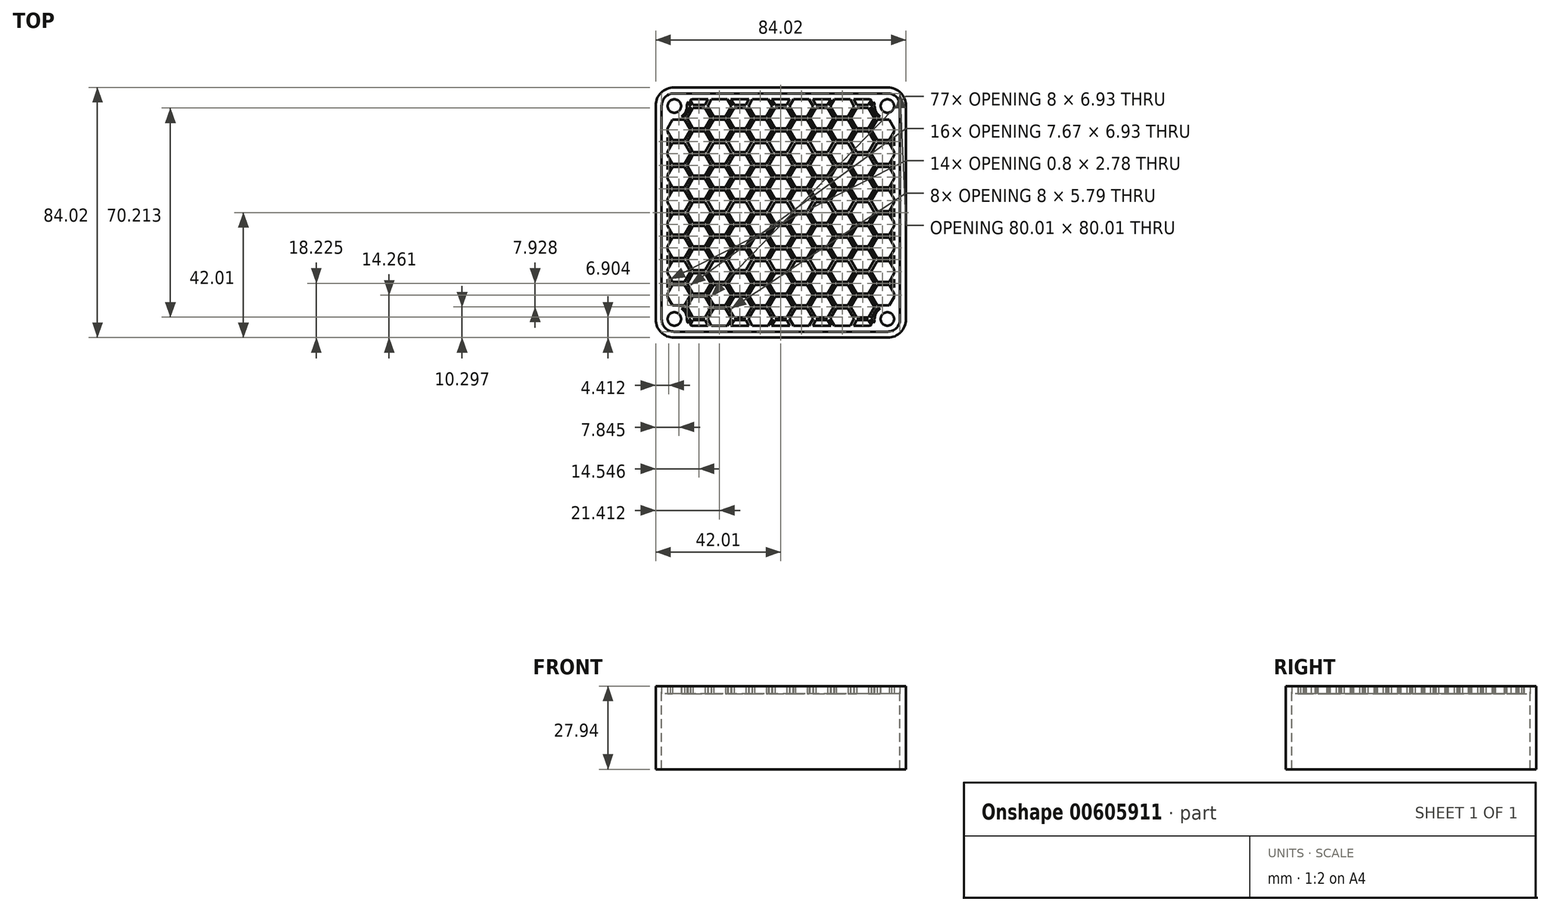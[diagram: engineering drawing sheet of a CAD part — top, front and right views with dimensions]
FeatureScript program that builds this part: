
annotation { "Feature Type Name" : "Feature", "Feature Type Description" : "" }
export const myFeature = defineFeature(function(context is Context, id is Id, definition is map)
    precondition{}
    {
        {
            var Q0;
            Q0=qCreatedBy(makeId("Top.planeOp"),FACE);
            var sketch = newSketch(context, id + "F0", { "sketchPlane" : qUnion([Q0])});
            skLineSegment(sketch, "E0", {"start": v(11.73, 28.25) * mm, "end": v(9.73, 31.71) * mm});
            skLineSegment(sketch, "E1", {"start": v(-16.6, 27.75) * mm, "end": v(-18.6, 24.28) * mm});
            skLineSegment(sketch, "E2", {"start": v(-2, -3.46) * mm, "end": v(2, -3.46) * mm});
            skLineSegment(sketch, "E3", {"start": v(2, -3.46) * mm, "end": v(4, 0) * mm});
            skLineSegment(sketch, "E4", {"start": v(4, 0) * mm, "end": v(2, 3.46) * mm});
            skLineSegment(sketch, "E5", {"start": v(2, 3.46) * mm, "end": v(-2, 3.46) * mm});
            skLineSegment(sketch, "E6", {"start": v(-2, 3.46) * mm, "end": v(-4, 0) * mm});
            skLineSegment(sketch, "E7", {"start": v(-4, 0) * mm, "end": v(-2, -3.46) * mm});
            skLineSegment(sketch, "E8", {"start": v(-2.87, 3.96) * mm, "end": v(-4.87, 0.5) * mm});
            skLineSegment(sketch, "E9", {"start": v(-4.87, -0.5) * mm, "end": v(-2.87, -3.96) * mm});
            skLineSegment(sketch, "E10", {"start": v(-2, 4.46) * mm, "end": v(2, 4.46) * mm});
            skLineSegment(sketch, "E11", {"start": v(2, 4.46) * mm, "end": v(4, 7.93) * mm});
            skLineSegment(sketch, "E12", {"start": v(4, 7.93) * mm, "end": v(2, 11.4) * mm});
            skLineSegment(sketch, "E13", {"start": v(2, 11.4) * mm, "end": v(-2, 11.4) * mm});
            skLineSegment(sketch, "E14", {"start": v(-2, 11.4) * mm, "end": v(-4, 7.93) * mm});
            skLineSegment(sketch, "E15", {"start": v(-4, 7.93) * mm, "end": v(-2, 4.46) * mm});
            skLineSegment(sketch, "E16", {"start": v(-2, 12.4) * mm, "end": v(2, 12.4) * mm});
            skLineSegment(sketch, "E17", {"start": v(2, 12.4) * mm, "end": v(4, 15.86) * mm});
            skLineSegment(sketch, "E18", {"start": v(4, 15.86) * mm, "end": v(2, 19.32) * mm});
            skLineSegment(sketch, "E19", {"start": v(2, 19.32) * mm, "end": v(-2, 19.32) * mm});
            skLineSegment(sketch, "E20", {"start": v(-2, 19.32) * mm, "end": v(-4, 15.86) * mm});
            skLineSegment(sketch, "E21", {"start": v(-4, 15.86) * mm, "end": v(-2, 12.4) * mm});
            skLineSegment(sketch, "E22", {"start": v(-2, 20.32) * mm, "end": v(2, 20.32) * mm});
            skLineSegment(sketch, "E23", {"start": v(2, 20.32) * mm, "end": v(4, 23.78) * mm});
            skLineSegment(sketch, "E24", {"start": v(4, 23.78) * mm, "end": v(2, 27.25) * mm});
            skLineSegment(sketch, "E25", {"start": v(2, 27.25) * mm, "end": v(-2, 27.25) * mm});
            skLineSegment(sketch, "E26", {"start": v(-2, 27.25) * mm, "end": v(-4, 23.78) * mm});
            skLineSegment(sketch, "E27", {"start": v(-4, 23.78) * mm, "end": v(-2, 20.32) * mm});
            skLineSegment(sketch, "E28", {"start": v(-2, 28.25) * mm, "end": v(2, 28.25) * mm});
            skLineSegment(sketch, "E29", {"start": v(2, 28.25) * mm, "end": v(4, 31.71) * mm});
            skLineSegment(sketch, "E30", {"start": v(4, 31.71) * mm, "end": v(2, 35.18) * mm});
            skLineSegment(sketch, "E31", {"start": v(2, 35.18) * mm, "end": v(-2, 35.18) * mm});
            skLineSegment(sketch, "E32", {"start": v(-2, 35.18) * mm, "end": v(-4, 31.71) * mm});
            skLineSegment(sketch, "E33", {"start": v(-4, 31.71) * mm, "end": v(-2, 28.25) * mm});
            skLineSegment(sketch, "E34", {"start": v(-2, 36.18) * mm, "end": v(2, 36.18) * mm});
            skLineSegment(sketch, "E35", {"start": v(-2, -11.4) * mm, "end": v(2, -11.4) * mm});
            skLineSegment(sketch, "E36", {"start": v(2, -11.4) * mm, "end": v(4, -7.93) * mm});
            skLineSegment(sketch, "E37", {"start": v(4, -7.93) * mm, "end": v(2, -4.46) * mm});
            skLineSegment(sketch, "E38", {"start": v(2, -4.46) * mm, "end": v(-2, -4.46) * mm});
            skLineSegment(sketch, "E39", {"start": v(-2, -4.46) * mm, "end": v(-4, -7.93) * mm});
            skLineSegment(sketch, "E40", {"start": v(-4, -7.93) * mm, "end": v(-2, -11.4) * mm});
            skLineSegment(sketch, "E41", {"start": v(-2, -19.32) * mm, "end": v(2, -19.32) * mm});
            skLineSegment(sketch, "E42", {"start": v(2, -19.32) * mm, "end": v(4, -15.86) * mm});
            skLineSegment(sketch, "E43", {"start": v(4, -15.86) * mm, "end": v(2, -12.4) * mm});
            skLineSegment(sketch, "E44", {"start": v(2, -12.4) * mm, "end": v(-2, -12.4) * mm});
            skLineSegment(sketch, "E45", {"start": v(-2, -12.4) * mm, "end": v(-4, -15.86) * mm});
            skLineSegment(sketch, "E46", {"start": v(-4, -15.86) * mm, "end": v(-2, -19.32) * mm});
            skLineSegment(sketch, "E47", {"start": v(-2, -27.25) * mm, "end": v(2, -27.25) * mm});
            skLineSegment(sketch, "E48", {"start": v(2, -27.25) * mm, "end": v(4, -23.78) * mm});
            skLineSegment(sketch, "E49", {"start": v(4, -23.78) * mm, "end": v(2, -20.32) * mm});
            skLineSegment(sketch, "E50", {"start": v(2, -20.32) * mm, "end": v(-2, -20.32) * mm});
            skLineSegment(sketch, "E51", {"start": v(-2, -20.32) * mm, "end": v(-4, -23.78) * mm});
            skLineSegment(sketch, "E52", {"start": v(-4, -23.78) * mm, "end": v(-2, -27.25) * mm});
            skLineSegment(sketch, "E53", {"start": v(-2, -35.18) * mm, "end": v(2, -35.18) * mm});
            skLineSegment(sketch, "E54", {"start": v(2, -35.18) * mm, "end": v(4, -31.71) * mm});
            skLineSegment(sketch, "E55", {"start": v(4, -31.71) * mm, "end": v(2, -28.25) * mm});
            skLineSegment(sketch, "E56", {"start": v(2, -28.25) * mm, "end": v(-2, -28.25) * mm});
            skLineSegment(sketch, "E57", {"start": v(-2, -28.25) * mm, "end": v(-4, -31.71) * mm});
            skLineSegment(sketch, "E58", {"start": v(-4, -31.71) * mm, "end": v(-2, -35.18) * mm});
            skLineSegment(sketch, "E59", {"start": v(2, -36.18) * mm, "end": v(-2, -36.18) * mm});
            skLineSegment(sketch, "E60", {"start": v(4.87, -7.43) * mm, "end": v(8.87, -7.43) * mm});
            skLineSegment(sketch, "E61", {"start": v(8.87, -7.43) * mm, "end": v(10.87, -3.96) * mm});
            skLineSegment(sketch, "E62", {"start": v(10.87, -3.96) * mm, "end": v(8.87, -0.5) * mm});
            skLineSegment(sketch, "E63", {"start": v(8.87, -0.5) * mm, "end": v(4.87, -0.5) * mm});
            skLineSegment(sketch, "E64", {"start": v(4.87, -0.5) * mm, "end": v(2.87, -3.96) * mm});
            skLineSegment(sketch, "E65", {"start": v(2.87, -3.96) * mm, "end": v(4.87, -7.43) * mm});
            skLineSegment(sketch, "E66", {"start": v(4, 0) * mm, "end": v(2, -3.46) * mm});
            skLineSegment(sketch, "E67", {"start": v(2, -4.46) * mm, "end": v(4, -7.93) * mm});
            skLineSegment(sketch, "E68", {"start": v(4.87, 0.5) * mm, "end": v(8.87, 0.5) * mm});
            skLineSegment(sketch, "E69", {"start": v(8.87, 0.5) * mm, "end": v(10.87, 3.96) * mm});
            skLineSegment(sketch, "E70", {"start": v(10.87, 3.96) * mm, "end": v(8.87, 7.43) * mm});
            skLineSegment(sketch, "E71", {"start": v(8.87, 7.43) * mm, "end": v(4.87, 7.43) * mm});
            skLineSegment(sketch, "E72", {"start": v(4.87, 7.43) * mm, "end": v(2.87, 3.96) * mm});
            skLineSegment(sketch, "E73", {"start": v(2.87, 3.96) * mm, "end": v(4.87, 0.5) * mm});
            skLineSegment(sketch, "E74", {"start": v(4.87, 8.43) * mm, "end": v(8.87, 8.43) * mm});
            skLineSegment(sketch, "E75", {"start": v(8.87, 8.43) * mm, "end": v(10.87, 11.9) * mm});
            skLineSegment(sketch, "E76", {"start": v(10.87, 11.9) * mm, "end": v(8.87, 15.36) * mm});
            skLineSegment(sketch, "E77", {"start": v(8.87, 15.36) * mm, "end": v(4.87, 15.36) * mm});
            skLineSegment(sketch, "E78", {"start": v(4.87, 15.36) * mm, "end": v(2.87, 11.9) * mm});
            skLineSegment(sketch, "E79", {"start": v(2.87, 11.9) * mm, "end": v(4.87, 8.43) * mm});
            skLineSegment(sketch, "E80", {"start": v(4.87, 16.36) * mm, "end": v(8.87, 16.36) * mm});
            skLineSegment(sketch, "E81", {"start": v(8.87, 16.36) * mm, "end": v(10.87, 19.82) * mm});
            skLineSegment(sketch, "E82", {"start": v(10.87, 19.82) * mm, "end": v(8.87, 23.28) * mm});
            skLineSegment(sketch, "E83", {"start": v(8.87, 23.28) * mm, "end": v(4.87, 23.28) * mm});
            skLineSegment(sketch, "E84", {"start": v(4.87, 23.28) * mm, "end": v(2.87, 19.82) * mm});
            skLineSegment(sketch, "E85", {"start": v(2.87, 19.82) * mm, "end": v(4.87, 16.36) * mm});
            skLineSegment(sketch, "E86", {"start": v(4.87, 24.28) * mm, "end": v(8.87, 24.28) * mm});
            skLineSegment(sketch, "E87", {"start": v(8.87, 24.28) * mm, "end": v(10.87, 27.75) * mm});
            skLineSegment(sketch, "E88", {"start": v(10.87, 27.75) * mm, "end": v(8.87, 31.21) * mm});
            skLineSegment(sketch, "E89", {"start": v(8.87, 31.21) * mm, "end": v(4.87, 31.21) * mm});
            skLineSegment(sketch, "E90", {"start": v(4.87, 31.21) * mm, "end": v(2.87, 27.75) * mm});
            skLineSegment(sketch, "E91", {"start": v(2.87, 27.75) * mm, "end": v(4.87, 24.28) * mm});
            skLineSegment(sketch, "E92", {"start": v(4.87, 32.21) * mm, "end": v(8.87, 32.21) * mm});
            skLineSegment(sketch, "E93", {"start": v(8.87, 32.21) * mm, "end": v(10.87, 35.68) * mm});
            skLineSegment(sketch, "E94", {"start": v(2.87, 35.68) * mm, "end": v(4.87, 32.21) * mm});
            skLineSegment(sketch, "E95", {"start": v(4.87, -15.36) * mm, "end": v(8.87, -15.36) * mm});
            skLineSegment(sketch, "E96", {"start": v(8.87, -15.36) * mm, "end": v(10.87, -11.9) * mm});
            skLineSegment(sketch, "E97", {"start": v(10.87, -11.9) * mm, "end": v(8.87, -8.43) * mm});
            skLineSegment(sketch, "E98", {"start": v(8.87, -8.43) * mm, "end": v(4.87, -8.43) * mm});
            skLineSegment(sketch, "E99", {"start": v(4.87, -8.43) * mm, "end": v(2.87, -11.9) * mm});
            skLineSegment(sketch, "E100", {"start": v(2.87, -11.9) * mm, "end": v(4.87, -15.36) * mm});
            skLineSegment(sketch, "E101", {"start": v(4.87, -23.28) * mm, "end": v(8.87, -23.28) * mm});
            skLineSegment(sketch, "E102", {"start": v(8.87, -23.28) * mm, "end": v(10.87, -19.82) * mm});
            skLineSegment(sketch, "E103", {"start": v(10.87, -19.82) * mm, "end": v(8.87, -16.36) * mm});
            skLineSegment(sketch, "E104", {"start": v(8.87, -16.36) * mm, "end": v(4.87, -16.36) * mm});
            skLineSegment(sketch, "E105", {"start": v(4.87, -16.36) * mm, "end": v(2.87, -19.82) * mm});
            skLineSegment(sketch, "E106", {"start": v(2.87, -19.82) * mm, "end": v(4.87, -23.28) * mm});
            skLineSegment(sketch, "E107", {"start": v(4.87, -31.21) * mm, "end": v(8.87, -31.21) * mm});
            skLineSegment(sketch, "E108", {"start": v(8.87, -31.21) * mm, "end": v(10.87, -27.75) * mm});
            skLineSegment(sketch, "E109", {"start": v(10.87, -27.75) * mm, "end": v(8.87, -24.28) * mm});
            skLineSegment(sketch, "E110", {"start": v(8.87, -24.28) * mm, "end": v(4.87, -24.28) * mm});
            skLineSegment(sketch, "E111", {"start": v(4.87, -24.28) * mm, "end": v(2.87, -27.75) * mm});
            skLineSegment(sketch, "E112", {"start": v(2.87, -27.75) * mm, "end": v(4.87, -31.21) * mm});
            skLineSegment(sketch, "E113", {"start": v(10.87, -35.68) * mm, "end": v(8.87, -32.21) * mm});
            skLineSegment(sketch, "E114", {"start": v(8.87, -32.21) * mm, "end": v(4.87, -32.21) * mm});
            skLineSegment(sketch, "E115", {"start": v(4.87, -32.21) * mm, "end": v(2.87, -35.68) * mm});
            skLineSegment(sketch, "E116", {"start": v(-15.73, -3.46) * mm, "end": v(-11.73, -3.46) * mm});
            skLineSegment(sketch, "E117", {"start": v(-11.73, -3.46) * mm, "end": v(-9.73, 0) * mm});
            skLineSegment(sketch, "E118", {"start": v(-9.73, 0) * mm, "end": v(-11.73, 3.46) * mm});
            skLineSegment(sketch, "E119", {"start": v(-11.73, 3.46) * mm, "end": v(-15.73, 3.46) * mm});
            skLineSegment(sketch, "E120", {"start": v(-15.73, 3.46) * mm, "end": v(-17.73, 0) * mm});
            skLineSegment(sketch, "E121", {"start": v(-17.73, 0) * mm, "end": v(-15.73, -3.46) * mm});
            skLineSegment(sketch, "E122", {"start": v(-15.73, 4.46) * mm, "end": v(-11.73, 4.46) * mm});
            skLineSegment(sketch, "E123", {"start": v(-11.73, 4.46) * mm, "end": v(-9.73, 7.93) * mm});
            skLineSegment(sketch, "E124", {"start": v(-9.73, 7.93) * mm, "end": v(-11.73, 11.4) * mm});
            skLineSegment(sketch, "E125", {"start": v(-11.73, 11.4) * mm, "end": v(-15.73, 11.4) * mm});
            skLineSegment(sketch, "E126", {"start": v(-15.73, 11.4) * mm, "end": v(-17.73, 7.93) * mm});
            skLineSegment(sketch, "E127", {"start": v(-17.73, 7.93) * mm, "end": v(-15.73, 4.46) * mm});
            skLineSegment(sketch, "E128", {"start": v(-15.73, 12.4) * mm, "end": v(-11.73, 12.4) * mm});
            skLineSegment(sketch, "E129", {"start": v(-11.73, 12.4) * mm, "end": v(-9.73, 15.86) * mm});
            skLineSegment(sketch, "E130", {"start": v(-9.73, 15.86) * mm, "end": v(-11.73, 19.32) * mm});
            skLineSegment(sketch, "E131", {"start": v(-11.73, 19.32) * mm, "end": v(-15.73, 19.32) * mm});
            skLineSegment(sketch, "E132", {"start": v(-15.73, 19.32) * mm, "end": v(-17.73, 15.86) * mm});
            skLineSegment(sketch, "E133", {"start": v(-17.73, 15.86) * mm, "end": v(-15.73, 12.4) * mm});
            skLineSegment(sketch, "E134", {"start": v(-15.73, 20.32) * mm, "end": v(-11.73, 20.32) * mm});
            skLineSegment(sketch, "E135", {"start": v(-11.73, 20.32) * mm, "end": v(-9.73, 23.78) * mm});
            skLineSegment(sketch, "E136", {"start": v(-9.73, 23.78) * mm, "end": v(-11.73, 27.25) * mm});
            skLineSegment(sketch, "E137", {"start": v(-11.73, 27.25) * mm, "end": v(-15.73, 27.25) * mm});
            skLineSegment(sketch, "E138", {"start": v(-15.73, 27.25) * mm, "end": v(-17.73, 23.78) * mm});
            skLineSegment(sketch, "E139", {"start": v(-17.73, 23.78) * mm, "end": v(-15.73, 20.32) * mm});
            skLineSegment(sketch, "E140", {"start": v(-15.73, 28.25) * mm, "end": v(-11.73, 28.25) * mm});
            skLineSegment(sketch, "E141", {"start": v(-11.73, 28.25) * mm, "end": v(-9.73, 31.71) * mm});
            skLineSegment(sketch, "E142", {"start": v(-9.73, 31.71) * mm, "end": v(-11.73, 35.18) * mm});
            skLineSegment(sketch, "E143", {"start": v(-11.73, 35.18) * mm, "end": v(-15.73, 35.18) * mm});
            skLineSegment(sketch, "E144", {"start": v(-15.73, 35.18) * mm, "end": v(-17.73, 31.71) * mm});
            skLineSegment(sketch, "E145", {"start": v(-17.73, 31.71) * mm, "end": v(-15.73, 28.25) * mm});
            skLineSegment(sketch, "E146", {"start": v(-15.73, 36.18) * mm, "end": v(-11.73, 36.18) * mm});
            skLineSegment(sketch, "E147", {"start": v(-15.73, -11.4) * mm, "end": v(-11.73, -11.4) * mm});
            skLineSegment(sketch, "E148", {"start": v(-11.73, -11.4) * mm, "end": v(-9.73, -7.93) * mm});
            skLineSegment(sketch, "E149", {"start": v(-9.73, -7.93) * mm, "end": v(-11.73, -4.46) * mm});
            skLineSegment(sketch, "E150", {"start": v(-11.73, -4.46) * mm, "end": v(-15.73, -4.46) * mm});
            skLineSegment(sketch, "E151", {"start": v(-15.73, -4.46) * mm, "end": v(-17.73, -7.93) * mm});
            skLineSegment(sketch, "E152", {"start": v(-17.73, -7.93) * mm, "end": v(-15.73, -11.4) * mm});
            skLineSegment(sketch, "E153", {"start": v(-15.73, -19.32) * mm, "end": v(-11.73, -19.32) * mm});
            skLineSegment(sketch, "E154", {"start": v(-11.73, -19.32) * mm, "end": v(-9.73, -15.86) * mm});
            skLineSegment(sketch, "E155", {"start": v(-9.73, -15.86) * mm, "end": v(-11.73, -12.4) * mm});
            skLineSegment(sketch, "E156", {"start": v(-11.73, -12.4) * mm, "end": v(-15.73, -12.4) * mm});
            skLineSegment(sketch, "E157", {"start": v(-15.73, -12.4) * mm, "end": v(-17.73, -15.86) * mm});
            skLineSegment(sketch, "E158", {"start": v(-17.73, -15.86) * mm, "end": v(-15.73, -19.32) * mm});
            skLineSegment(sketch, "E159", {"start": v(-15.73, -27.25) * mm, "end": v(-11.73, -27.25) * mm});
            skLineSegment(sketch, "E160", {"start": v(-11.73, -27.25) * mm, "end": v(-9.73, -23.78) * mm});
            skLineSegment(sketch, "E161", {"start": v(-9.73, -23.78) * mm, "end": v(-11.73, -20.32) * mm});
            skLineSegment(sketch, "E162", {"start": v(-11.73, -20.32) * mm, "end": v(-15.73, -20.32) * mm});
            skLineSegment(sketch, "E163", {"start": v(-15.73, -20.32) * mm, "end": v(-17.73, -23.78) * mm});
            skLineSegment(sketch, "E164", {"start": v(-17.73, -23.78) * mm, "end": v(-15.73, -27.25) * mm});
            skLineSegment(sketch, "E165", {"start": v(-15.73, -35.18) * mm, "end": v(-11.73, -35.18) * mm});
            skLineSegment(sketch, "E166", {"start": v(-11.73, -35.18) * mm, "end": v(-9.73, -31.71) * mm});
            skLineSegment(sketch, "E167", {"start": v(-9.73, -31.71) * mm, "end": v(-11.73, -28.25) * mm});
            skLineSegment(sketch, "E168", {"start": v(-11.73, -28.25) * mm, "end": v(-15.73, -28.25) * mm});
            skLineSegment(sketch, "E169", {"start": v(-15.73, -28.25) * mm, "end": v(-17.73, -31.71) * mm});
            skLineSegment(sketch, "E170", {"start": v(-17.73, -31.71) * mm, "end": v(-15.73, -35.18) * mm});
            skLineSegment(sketch, "E171", {"start": v(-11.73, -36.18) * mm, "end": v(-15.73, -36.18) * mm});
            skLineSegment(sketch, "E172", {"start": v(-8.87, -7.43) * mm, "end": v(-4.87, -7.43) * mm});
            skLineSegment(sketch, "E173", {"start": v(-4.87, -7.43) * mm, "end": v(-2.87, -3.96) * mm});
            skLineSegment(sketch, "E174", {"start": v(-4.87, -0.5) * mm, "end": v(-8.87, -0.5) * mm});
            skLineSegment(sketch, "E175", {"start": v(-8.87, -0.5) * mm, "end": v(-10.87, -3.96) * mm});
            skLineSegment(sketch, "E176", {"start": v(-10.87, -3.96) * mm, "end": v(-8.87, -7.43) * mm});
            skLineSegment(sketch, "E177", {"start": v(-9.73, 0) * mm, "end": v(-11.73, -3.46) * mm});
            skLineSegment(sketch, "E178", {"start": v(-11.73, -4.46) * mm, "end": v(-9.73, -7.93) * mm});
            skLineSegment(sketch, "E179", {"start": v(-8.87, 0.5) * mm, "end": v(-4.87, 0.5) * mm});
            skLineSegment(sketch, "E180", {"start": v(-2.87, 3.96) * mm, "end": v(-4.87, 7.43) * mm});
            skLineSegment(sketch, "E181", {"start": v(-4.87, 7.43) * mm, "end": v(-8.87, 7.43) * mm});
            skLineSegment(sketch, "E182", {"start": v(-8.87, 7.43) * mm, "end": v(-10.87, 3.96) * mm});
            skLineSegment(sketch, "E183", {"start": v(-10.87, 3.96) * mm, "end": v(-8.87, 0.5) * mm});
            skLineSegment(sketch, "E184", {"start": v(-8.87, 8.43) * mm, "end": v(-4.87, 8.43) * mm});
            skLineSegment(sketch, "E185", {"start": v(-4.87, 8.43) * mm, "end": v(-2.87, 11.9) * mm});
            skLineSegment(sketch, "E186", {"start": v(-2.87, 11.9) * mm, "end": v(-4.87, 15.36) * mm});
            skLineSegment(sketch, "E187", {"start": v(-4.87, 15.36) * mm, "end": v(-8.87, 15.36) * mm});
            skLineSegment(sketch, "E188", {"start": v(-8.87, 15.36) * mm, "end": v(-10.87, 11.9) * mm});
            skLineSegment(sketch, "E189", {"start": v(-10.87, 11.9) * mm, "end": v(-8.87, 8.43) * mm});
            skLineSegment(sketch, "E190", {"start": v(-8.87, 16.36) * mm, "end": v(-4.87, 16.36) * mm});
            skLineSegment(sketch, "E191", {"start": v(-4.87, 16.36) * mm, "end": v(-2.87, 19.82) * mm});
            skLineSegment(sketch, "E192", {"start": v(-2.87, 19.82) * mm, "end": v(-4.87, 23.28) * mm});
            skLineSegment(sketch, "E193", {"start": v(-4.87, 23.28) * mm, "end": v(-8.87, 23.28) * mm});
            skLineSegment(sketch, "E194", {"start": v(-8.87, 23.28) * mm, "end": v(-10.87, 19.82) * mm});
            skLineSegment(sketch, "E195", {"start": v(-10.87, 19.82) * mm, "end": v(-8.87, 16.36) * mm});
            skLineSegment(sketch, "E196", {"start": v(-8.87, 24.28) * mm, "end": v(-4.87, 24.28) * mm});
            skLineSegment(sketch, "E197", {"start": v(-4.87, 24.28) * mm, "end": v(-2.87, 27.75) * mm});
            skLineSegment(sketch, "E198", {"start": v(-2.87, 27.75) * mm, "end": v(-4.87, 31.21) * mm});
            skLineSegment(sketch, "E199", {"start": v(-4.87, 31.21) * mm, "end": v(-8.87, 31.21) * mm});
            skLineSegment(sketch, "E200", {"start": v(-8.87, 31.21) * mm, "end": v(-10.87, 27.75) * mm});
            skLineSegment(sketch, "E201", {"start": v(-10.87, 27.75) * mm, "end": v(-8.87, 24.28) * mm});
            skLineSegment(sketch, "E202", {"start": v(-8.87, 32.21) * mm, "end": v(-4.87, 32.21) * mm});
            skLineSegment(sketch, "E203", {"start": v(-4.87, 32.21) * mm, "end": v(-2.87, 35.68) * mm});
            skLineSegment(sketch, "E204", {"start": v(-10.87, 35.68) * mm, "end": v(-8.87, 32.21) * mm});
            skLineSegment(sketch, "E205", {"start": v(-8.87, -15.36) * mm, "end": v(-4.87, -15.36) * mm});
            skLineSegment(sketch, "E206", {"start": v(-4.87, -15.36) * mm, "end": v(-2.87, -11.9) * mm});
            skLineSegment(sketch, "E207", {"start": v(-2.87, -11.9) * mm, "end": v(-4.87, -8.43) * mm});
            skLineSegment(sketch, "E208", {"start": v(-4.87, -8.43) * mm, "end": v(-8.87, -8.43) * mm});
            skLineSegment(sketch, "E209", {"start": v(-8.87, -8.43) * mm, "end": v(-10.87, -11.9) * mm});
            skLineSegment(sketch, "E210", {"start": v(-10.87, -11.9) * mm, "end": v(-8.87, -15.36) * mm});
            skLineSegment(sketch, "E211", {"start": v(-8.87, -23.28) * mm, "end": v(-4.87, -23.28) * mm});
            skLineSegment(sketch, "E212", {"start": v(-4.87, -23.28) * mm, "end": v(-2.87, -19.82) * mm});
            skLineSegment(sketch, "E213", {"start": v(-2.87, -19.82) * mm, "end": v(-4.87, -16.36) * mm});
            skLineSegment(sketch, "E214", {"start": v(-4.87, -16.36) * mm, "end": v(-8.87, -16.36) * mm});
            skLineSegment(sketch, "E215", {"start": v(-8.87, -16.36) * mm, "end": v(-10.87, -19.82) * mm});
            skLineSegment(sketch, "E216", {"start": v(-10.87, -19.82) * mm, "end": v(-8.87, -23.28) * mm});
            skLineSegment(sketch, "E217", {"start": v(-8.87, -31.21) * mm, "end": v(-4.87, -31.21) * mm});
            skLineSegment(sketch, "E218", {"start": v(-4.87, -31.21) * mm, "end": v(-2.87, -27.75) * mm});
            skLineSegment(sketch, "E219", {"start": v(-2.87, -27.75) * mm, "end": v(-4.87, -24.28) * mm});
            skLineSegment(sketch, "E220", {"start": v(-4.87, -24.28) * mm, "end": v(-8.87, -24.28) * mm});
            skLineSegment(sketch, "E221", {"start": v(-8.87, -24.28) * mm, "end": v(-10.87, -27.75) * mm});
            skLineSegment(sketch, "E222", {"start": v(-10.87, -27.75) * mm, "end": v(-8.87, -31.21) * mm});
            skLineSegment(sketch, "E223", {"start": v(-2.87, -35.68) * mm, "end": v(-4.87, -32.21) * mm});
            skLineSegment(sketch, "E224", {"start": v(-4.87, -32.21) * mm, "end": v(-8.87, -32.21) * mm});
            skLineSegment(sketch, "E225", {"start": v(-8.87, -32.21) * mm, "end": v(-10.87, -35.68) * mm});
            skLineSegment(sketch, "E226", {"start": v(-29.46, -3.46) * mm, "end": v(-25.46, -3.46) * mm});
            skLineSegment(sketch, "E227", {"start": v(-25.46, -3.46) * mm, "end": v(-23.46, 0) * mm});
            skLineSegment(sketch, "E228", {"start": v(-23.46, 0) * mm, "end": v(-25.46, 3.46) * mm});
            skLineSegment(sketch, "E229", {"start": v(-25.46, 3.46) * mm, "end": v(-29.46, 3.46) * mm});
            skLineSegment(sketch, "E230", {"start": v(-29.46, 3.46) * mm, "end": v(-31.46, 0) * mm});
            skLineSegment(sketch, "E231", {"start": v(-31.46, 0) * mm, "end": v(-29.46, -3.46) * mm});
            skLineSegment(sketch, "E232", {"start": v(-30.33, 3.96) * mm, "end": v(-32.33, 0.5) * mm});
            skLineSegment(sketch, "E233", {"start": v(-32.33, -0.5) * mm, "end": v(-30.33, -3.96) * mm});
            skLineSegment(sketch, "E234", {"start": v(-29.46, 4.46) * mm, "end": v(-25.46, 4.46) * mm});
            skLineSegment(sketch, "E235", {"start": v(-25.46, 4.46) * mm, "end": v(-23.46, 7.93) * mm});
            skLineSegment(sketch, "E236", {"start": v(-23.46, 7.93) * mm, "end": v(-25.46, 11.4) * mm});
            skLineSegment(sketch, "E237", {"start": v(-25.46, 11.4) * mm, "end": v(-29.46, 11.4) * mm});
            skLineSegment(sketch, "E238", {"start": v(-29.46, 11.4) * mm, "end": v(-31.46, 7.93) * mm});
            skLineSegment(sketch, "E239", {"start": v(-31.46, 7.93) * mm, "end": v(-29.46, 4.46) * mm});
            skLineSegment(sketch, "E240", {"start": v(-29.46, 12.4) * mm, "end": v(-25.46, 12.4) * mm});
            skLineSegment(sketch, "E241", {"start": v(-25.46, 12.4) * mm, "end": v(-23.46, 15.86) * mm});
            skLineSegment(sketch, "E242", {"start": v(-23.46, 15.86) * mm, "end": v(-25.46, 19.32) * mm});
            skLineSegment(sketch, "E243", {"start": v(-25.46, 19.32) * mm, "end": v(-29.46, 19.32) * mm});
            skLineSegment(sketch, "E244", {"start": v(-29.46, 19.32) * mm, "end": v(-31.46, 15.86) * mm});
            skLineSegment(sketch, "E245", {"start": v(-31.46, 15.86) * mm, "end": v(-29.46, 12.4) * mm});
            skLineSegment(sketch, "E246", {"start": v(-29.46, 20.32) * mm, "end": v(-25.46, 20.32) * mm});
            skLineSegment(sketch, "E247", {"start": v(-25.46, 20.32) * mm, "end": v(-23.46, 23.78) * mm});
            skLineSegment(sketch, "E248", {"start": v(-23.46, 23.78) * mm, "end": v(-25.46, 27.25) * mm});
            skLineSegment(sketch, "E249", {"start": v(-25.46, 27.25) * mm, "end": v(-29.46, 27.25) * mm});
            skLineSegment(sketch, "E250", {"start": v(-29.46, 27.25) * mm, "end": v(-31.46, 23.78) * mm});
            skLineSegment(sketch, "E251", {"start": v(-31.46, 23.78) * mm, "end": v(-29.46, 20.32) * mm});
            skLineSegment(sketch, "E252", {"start": v(-29.46, 28.25) * mm, "end": v(-25.46, 28.25) * mm});
            skLineSegment(sketch, "E253", {"start": v(-25.46, 28.25) * mm, "end": v(-23.46, 31.71) * mm});
            skLineSegment(sketch, "E254", {"start": v(-23.46, 31.71) * mm, "end": v(-25.46, 35.18) * mm});
            skLineSegment(sketch, "E255", {"start": v(-25.46, 35.18) * mm, "end": v(-29.46, 35.18) * mm});
            skLineSegment(sketch, "E256", {"start": v(-29.46, 35.18) * mm, "end": v(-31.46, 31.71) * mm});
            skLineSegment(sketch, "E257", {"start": v(-31.46, 31.71) * mm, "end": v(-29.46, 28.25) * mm});
            skLineSegment(sketch, "E258", {"start": v(-29.46, 36.18) * mm, "end": v(-25.46, 36.18) * mm});
            skLineSegment(sketch, "E259", {"start": v(-29.46, -11.4) * mm, "end": v(-25.46, -11.4) * mm});
            skLineSegment(sketch, "E260", {"start": v(-25.46, -11.4) * mm, "end": v(-23.46, -7.93) * mm});
            skLineSegment(sketch, "E261", {"start": v(-23.46, -7.93) * mm, "end": v(-25.46, -4.46) * mm});
            skLineSegment(sketch, "E262", {"start": v(-25.46, -4.46) * mm, "end": v(-29.46, -4.46) * mm});
            skLineSegment(sketch, "E263", {"start": v(-29.46, -4.46) * mm, "end": v(-31.46, -7.93) * mm});
            skLineSegment(sketch, "E264", {"start": v(-31.46, -7.93) * mm, "end": v(-29.46, -11.4) * mm});
            skLineSegment(sketch, "E265", {"start": v(-29.46, -19.32) * mm, "end": v(-25.46, -19.32) * mm});
            skLineSegment(sketch, "E266", {"start": v(-25.46, -19.32) * mm, "end": v(-23.46, -15.86) * mm});
            skLineSegment(sketch, "E267", {"start": v(-23.46, -15.86) * mm, "end": v(-25.46, -12.4) * mm});
            skLineSegment(sketch, "E268", {"start": v(-25.46, -12.4) * mm, "end": v(-29.46, -12.4) * mm});
            skLineSegment(sketch, "E269", {"start": v(-29.46, -12.4) * mm, "end": v(-31.46, -15.86) * mm});
            skLineSegment(sketch, "E270", {"start": v(-31.46, -15.86) * mm, "end": v(-29.46, -19.32) * mm});
            skLineSegment(sketch, "E271", {"start": v(-29.46, -27.25) * mm, "end": v(-25.46, -27.25) * mm});
            skLineSegment(sketch, "E272", {"start": v(-25.46, -27.25) * mm, "end": v(-23.46, -23.78) * mm});
            skLineSegment(sketch, "E273", {"start": v(-23.46, -23.78) * mm, "end": v(-25.46, -20.32) * mm});
            skLineSegment(sketch, "E274", {"start": v(-25.46, -20.32) * mm, "end": v(-29.46, -20.32) * mm});
            skLineSegment(sketch, "E275", {"start": v(-29.46, -20.32) * mm, "end": v(-31.46, -23.78) * mm});
            skLineSegment(sketch, "E276", {"start": v(-31.46, -23.78) * mm, "end": v(-29.46, -27.25) * mm});
            skLineSegment(sketch, "E277", {"start": v(-29.46, -35.18) * mm, "end": v(-25.46, -35.18) * mm});
            skLineSegment(sketch, "E278", {"start": v(-25.46, -35.18) * mm, "end": v(-23.46, -31.71) * mm});
            skLineSegment(sketch, "E279", {"start": v(-23.46, -31.71) * mm, "end": v(-25.46, -28.25) * mm});
            skLineSegment(sketch, "E280", {"start": v(-25.46, -28.25) * mm, "end": v(-29.46, -28.25) * mm});
            skLineSegment(sketch, "E281", {"start": v(-29.46, -28.25) * mm, "end": v(-31.46, -31.71) * mm});
            skLineSegment(sketch, "E282", {"start": v(-31.46, -31.71) * mm, "end": v(-29.46, -35.18) * mm});
            skLineSegment(sketch, "E283", {"start": v(-25.46, -36.18) * mm, "end": v(-29.46, -36.18) * mm});
            skLineSegment(sketch, "E284", {"start": v(-22.6, -7.43) * mm, "end": v(-18.6, -7.43) * mm});
            skLineSegment(sketch, "E285", {"start": v(-18.6, -7.43) * mm, "end": v(-16.6, -3.96) * mm});
            skLineSegment(sketch, "E286", {"start": v(-16.6, -3.96) * mm, "end": v(-18.6, -0.5) * mm});
            skLineSegment(sketch, "E287", {"start": v(-18.6, -0.5) * mm, "end": v(-22.6, -0.5) * mm});
            skLineSegment(sketch, "E288", {"start": v(-22.6, -0.5) * mm, "end": v(-24.6, -3.96) * mm});
            skLineSegment(sketch, "E289", {"start": v(-24.6, -3.96) * mm, "end": v(-22.6, -7.43) * mm});
            skLineSegment(sketch, "E290", {"start": v(-25.46, -4.46) * mm, "end": v(-23.46, -7.93) * mm});
            skLineSegment(sketch, "E291", {"start": v(-22.6, 0.5) * mm, "end": v(-18.6, 0.5) * mm});
            skLineSegment(sketch, "E292", {"start": v(-18.6, 0.5) * mm, "end": v(-16.6, 3.96) * mm});
            skLineSegment(sketch, "E293", {"start": v(-16.6, 3.96) * mm, "end": v(-18.6, 7.43) * mm});
            skLineSegment(sketch, "E294", {"start": v(-18.6, 7.43) * mm, "end": v(-22.6, 7.43) * mm});
            skLineSegment(sketch, "E295", {"start": v(-22.6, 7.43) * mm, "end": v(-24.6, 3.96) * mm});
            skLineSegment(sketch, "E296", {"start": v(-24.6, 3.96) * mm, "end": v(-22.6, 0.5) * mm});
            skLineSegment(sketch, "E297", {"start": v(-22.6, 8.43) * mm, "end": v(-18.6, 8.43) * mm});
            skLineSegment(sketch, "E298", {"start": v(-18.6, 8.43) * mm, "end": v(-16.6, 11.9) * mm});
            skLineSegment(sketch, "E299", {"start": v(-16.6, 11.9) * mm, "end": v(-18.6, 15.36) * mm});
            skLineSegment(sketch, "E300", {"start": v(-18.6, 15.36) * mm, "end": v(-22.6, 15.36) * mm});
            skLineSegment(sketch, "E301", {"start": v(-22.6, 15.36) * mm, "end": v(-24.6, 11.9) * mm});
            skLineSegment(sketch, "E302", {"start": v(-24.6, 11.9) * mm, "end": v(-22.6, 8.43) * mm});
            skLineSegment(sketch, "E303", {"start": v(-22.6, 16.36) * mm, "end": v(-18.6, 16.36) * mm});
            skLineSegment(sketch, "E304", {"start": v(-18.6, 16.36) * mm, "end": v(-16.6, 19.82) * mm});
            skLineSegment(sketch, "E305", {"start": v(-16.6, 19.82) * mm, "end": v(-18.6, 23.28) * mm});
            skLineSegment(sketch, "E306", {"start": v(-18.6, 23.28) * mm, "end": v(-22.6, 23.28) * mm});
            skLineSegment(sketch, "E307", {"start": v(-22.6, 23.28) * mm, "end": v(-24.6, 19.82) * mm});
            skLineSegment(sketch, "E308", {"start": v(-24.6, 19.82) * mm, "end": v(-22.6, 16.36) * mm});
            skLineSegment(sketch, "E309", {"start": v(-22.6, 24.28) * mm, "end": v(-18.6, 24.28) * mm});
            skLineSegment(sketch, "E310", {"start": v(-18.6, 24.28) * mm, "end": v(-16.6, 27.75) * mm});
            skLineSegment(sketch, "E311", {"start": v(-16.6, 27.75) * mm, "end": v(-18.6, 31.21) * mm});
            skLineSegment(sketch, "E312", {"start": v(-18.6, 31.21) * mm, "end": v(-22.6, 31.21) * mm});
            skLineSegment(sketch, "E313", {"start": v(-22.6, 31.21) * mm, "end": v(-24.6, 27.75) * mm});
            skLineSegment(sketch, "E314", {"start": v(-24.6, 27.75) * mm, "end": v(-22.6, 24.28) * mm});
            skLineSegment(sketch, "E315", {"start": v(-22.6, 32.21) * mm, "end": v(-18.6, 32.21) * mm});
            skLineSegment(sketch, "E316", {"start": v(-18.6, 32.21) * mm, "end": v(-16.6, 35.68) * mm});
            skLineSegment(sketch, "E317", {"start": v(-24.6, 35.68) * mm, "end": v(-22.6, 32.21) * mm});
            skLineSegment(sketch, "E318", {"start": v(-22.6, -15.36) * mm, "end": v(-18.6, -15.36) * mm});
            skLineSegment(sketch, "E319", {"start": v(-18.6, -15.36) * mm, "end": v(-16.6, -11.9) * mm});
            skLineSegment(sketch, "E320", {"start": v(-16.6, -11.9) * mm, "end": v(-18.6, -8.43) * mm});
            skLineSegment(sketch, "E321", {"start": v(-18.6, -8.43) * mm, "end": v(-22.6, -8.43) * mm});
            skLineSegment(sketch, "E322", {"start": v(-22.6, -8.43) * mm, "end": v(-24.6, -11.9) * mm});
            skLineSegment(sketch, "E323", {"start": v(-24.6, -11.9) * mm, "end": v(-22.6, -15.36) * mm});
            skLineSegment(sketch, "E324", {"start": v(-22.6, -23.28) * mm, "end": v(-18.6, -23.28) * mm});
            skLineSegment(sketch, "E325", {"start": v(-18.6, -23.28) * mm, "end": v(-16.6, -19.82) * mm});
            skLineSegment(sketch, "E326", {"start": v(-16.6, -19.82) * mm, "end": v(-18.6, -16.36) * mm});
            skLineSegment(sketch, "E327", {"start": v(-18.6, -16.36) * mm, "end": v(-22.6, -16.36) * mm});
            skLineSegment(sketch, "E328", {"start": v(-22.6, -16.36) * mm, "end": v(-24.6, -19.82) * mm});
            skLineSegment(sketch, "E329", {"start": v(-24.6, -19.82) * mm, "end": v(-22.6, -23.28) * mm});
            skLineSegment(sketch, "E330", {"start": v(-22.6, -31.21) * mm, "end": v(-18.6, -31.21) * mm});
            skLineSegment(sketch, "E331", {"start": v(-18.6, -31.21) * mm, "end": v(-16.6, -27.75) * mm});
            skLineSegment(sketch, "E332", {"start": v(-16.6, -27.75) * mm, "end": v(-18.6, -24.28) * mm});
            skLineSegment(sketch, "E333", {"start": v(-18.6, -24.28) * mm, "end": v(-22.6, -24.28) * mm});
            skLineSegment(sketch, "E334", {"start": v(-22.6, -24.28) * mm, "end": v(-24.6, -27.75) * mm});
            skLineSegment(sketch, "E335", {"start": v(-24.6, -27.75) * mm, "end": v(-22.6, -31.21) * mm});
            skLineSegment(sketch, "E336", {"start": v(-16.6, -35.68) * mm, "end": v(-18.6, -32.21) * mm});
            skLineSegment(sketch, "E337", {"start": v(-18.6, -32.21) * mm, "end": v(-22.6, -32.21) * mm});
            skLineSegment(sketch, "E338", {"start": v(-22.6, -32.21) * mm, "end": v(-24.6, -35.68) * mm});
            skLineSegment(sketch, "E339", {"start": v(-36.33, -7.43) * mm, "end": v(-32.33, -7.43) * mm});
            skLineSegment(sketch, "E340", {"start": v(-32.33, -7.43) * mm, "end": v(-30.33, -3.96) * mm});
            skLineSegment(sketch, "E341", {"start": v(-32.33, -0.5) * mm, "end": v(-36.33, -0.5) * mm});
            skLineSegment(sketch, "E342", {"start": v(-36.33, 0.5) * mm, "end": v(-32.33, 0.5) * mm});
            skLineSegment(sketch, "E343", {"start": v(-30.33, 3.96) * mm, "end": v(-32.33, 7.43) * mm});
            skLineSegment(sketch, "E344", {"start": v(-32.33, 7.43) * mm, "end": v(-36.33, 7.43) * mm});
            skLineSegment(sketch, "E345", {"start": v(-36.33, 8.43) * mm, "end": v(-32.33, 8.43) * mm});
            skLineSegment(sketch, "E346", {"start": v(-32.33, 8.43) * mm, "end": v(-30.33, 11.9) * mm});
            skLineSegment(sketch, "E347", {"start": v(-30.33, 11.9) * mm, "end": v(-32.33, 15.36) * mm});
            skLineSegment(sketch, "E348", {"start": v(-32.33, 15.36) * mm, "end": v(-36.33, 15.36) * mm});
            skLineSegment(sketch, "E349", {"start": v(-36.33, 16.36) * mm, "end": v(-32.33, 16.36) * mm});
            skLineSegment(sketch, "E350", {"start": v(-32.33, 16.36) * mm, "end": v(-30.33, 19.82) * mm});
            skLineSegment(sketch, "E351", {"start": v(-30.33, 19.82) * mm, "end": v(-32.33, 23.28) * mm});
            skLineSegment(sketch, "E352", {"start": v(-32.33, 23.28) * mm, "end": v(-36.33, 23.28) * mm});
            skLineSegment(sketch, "E353", {"start": v(-36.33, 24.28) * mm, "end": v(-32.33, 24.28) * mm});
            skLineSegment(sketch, "E354", {"start": v(-32.33, 24.28) * mm, "end": v(-30.33, 27.75) * mm});
            skLineSegment(sketch, "E355", {"start": v(-30.33, 27.75) * mm, "end": v(-32.33, 31.21) * mm});
            skLineSegment(sketch, "E356", {"start": v(-32.33, 31.21) * mm, "end": v(-36.33, 31.21) * mm});
            skLineSegment(sketch, "E357", {"start": v(-32.33, 32.21) * mm, "end": v(-30.33, 35.68) * mm});
            skLineSegment(sketch, "E358", {"start": v(-36.33, -15.36) * mm, "end": v(-32.33, -15.36) * mm});
            skLineSegment(sketch, "E359", {"start": v(-32.33, -15.36) * mm, "end": v(-30.33, -11.9) * mm});
            skLineSegment(sketch, "E360", {"start": v(-30.33, -11.9) * mm, "end": v(-32.33, -8.43) * mm});
            skLineSegment(sketch, "E361", {"start": v(-32.33, -8.43) * mm, "end": v(-36.33, -8.43) * mm});
            skLineSegment(sketch, "E362", {"start": v(-36.33, -23.28) * mm, "end": v(-32.33, -23.28) * mm});
            skLineSegment(sketch, "E363", {"start": v(-32.33, -23.28) * mm, "end": v(-30.33, -19.82) * mm});
            skLineSegment(sketch, "E364", {"start": v(-30.33, -19.82) * mm, "end": v(-32.33, -16.36) * mm});
            skLineSegment(sketch, "E365", {"start": v(-32.33, -16.36) * mm, "end": v(-36.33, -16.36) * mm});
            skLineSegment(sketch, "E366", {"start": v(-36.33, -31.21) * mm, "end": v(-32.33, -31.21) * mm});
            skLineSegment(sketch, "E367", {"start": v(-32.33, -31.21) * mm, "end": v(-30.33, -27.75) * mm});
            skLineSegment(sketch, "E368", {"start": v(-30.33, -27.75) * mm, "end": v(-32.33, -24.28) * mm});
            skLineSegment(sketch, "E369", {"start": v(-32.33, -24.28) * mm, "end": v(-36.33, -24.28) * mm});
            skLineSegment(sketch, "E370", {"start": v(-30.33, -35.68) * mm, "end": v(-32.33, -32.21) * mm});
            skLineSegment(sketch, "E371", {"start": v(25.46, -3.46) * mm, "end": v(29.46, -3.46) * mm});
            skLineSegment(sketch, "E372", {"start": v(29.46, -3.46) * mm, "end": v(31.46, 0) * mm});
            skLineSegment(sketch, "E373", {"start": v(31.46, 0) * mm, "end": v(29.46, 3.46) * mm});
            skLineSegment(sketch, "E374", {"start": v(29.46, 3.46) * mm, "end": v(25.46, 3.46) * mm});
            skLineSegment(sketch, "E375", {"start": v(25.46, 3.46) * mm, "end": v(23.46, 0) * mm});
            skLineSegment(sketch, "E376", {"start": v(23.46, 0) * mm, "end": v(25.46, -3.46) * mm});
            skLineSegment(sketch, "E377", {"start": v(24.6, 3.96) * mm, "end": v(22.6, 0.5) * mm});
            skLineSegment(sketch, "E378", {"start": v(22.6, -0.5) * mm, "end": v(24.6, -3.96) * mm});
            skLineSegment(sketch, "E379", {"start": v(25.46, 4.46) * mm, "end": v(29.46, 4.46) * mm});
            skLineSegment(sketch, "E380", {"start": v(29.46, 4.46) * mm, "end": v(31.46, 7.93) * mm});
            skLineSegment(sketch, "E381", {"start": v(31.46, 7.93) * mm, "end": v(29.46, 11.4) * mm});
            skLineSegment(sketch, "E382", {"start": v(29.46, 11.4) * mm, "end": v(25.46, 11.4) * mm});
            skLineSegment(sketch, "E383", {"start": v(25.46, 11.4) * mm, "end": v(23.46, 7.93) * mm});
            skLineSegment(sketch, "E384", {"start": v(23.46, 7.93) * mm, "end": v(25.46, 4.46) * mm});
            skLineSegment(sketch, "E385", {"start": v(25.46, 12.4) * mm, "end": v(29.46, 12.4) * mm});
            skLineSegment(sketch, "E386", {"start": v(29.46, 12.4) * mm, "end": v(31.46, 15.86) * mm});
            skLineSegment(sketch, "E387", {"start": v(31.46, 15.86) * mm, "end": v(29.46, 19.32) * mm});
            skLineSegment(sketch, "E388", {"start": v(29.46, 19.32) * mm, "end": v(25.46, 19.32) * mm});
            skLineSegment(sketch, "E389", {"start": v(25.46, 19.32) * mm, "end": v(23.46, 15.86) * mm});
            skLineSegment(sketch, "E390", {"start": v(23.46, 15.86) * mm, "end": v(25.46, 12.4) * mm});
            skLineSegment(sketch, "E391", {"start": v(25.46, 20.32) * mm, "end": v(29.46, 20.32) * mm});
            skLineSegment(sketch, "E392", {"start": v(29.46, 20.32) * mm, "end": v(31.46, 23.78) * mm});
            skLineSegment(sketch, "E393", {"start": v(31.46, 23.78) * mm, "end": v(29.46, 27.25) * mm});
            skLineSegment(sketch, "E394", {"start": v(29.46, 27.25) * mm, "end": v(25.46, 27.25) * mm});
            skLineSegment(sketch, "E395", {"start": v(25.46, 27.25) * mm, "end": v(23.46, 23.78) * mm});
            skLineSegment(sketch, "E396", {"start": v(23.46, 23.78) * mm, "end": v(25.46, 20.32) * mm});
            skLineSegment(sketch, "E397", {"start": v(25.46, 28.25) * mm, "end": v(29.46, 28.25) * mm});
            skLineSegment(sketch, "E398", {"start": v(29.46, 28.25) * mm, "end": v(31.46, 31.71) * mm});
            skLineSegment(sketch, "E399", {"start": v(31.46, 31.71) * mm, "end": v(29.46, 35.18) * mm});
            skLineSegment(sketch, "E400", {"start": v(29.46, 35.18) * mm, "end": v(25.46, 35.18) * mm});
            skLineSegment(sketch, "E401", {"start": v(25.46, 35.18) * mm, "end": v(23.46, 31.71) * mm});
            skLineSegment(sketch, "E402", {"start": v(23.46, 31.71) * mm, "end": v(25.46, 28.25) * mm});
            skLineSegment(sketch, "E403", {"start": v(25.46, 36.18) * mm, "end": v(29.46, 36.18) * mm});
            skLineSegment(sketch, "E404", {"start": v(25.46, -11.4) * mm, "end": v(29.46, -11.4) * mm});
            skLineSegment(sketch, "E405", {"start": v(29.46, -11.4) * mm, "end": v(31.46, -7.93) * mm});
            skLineSegment(sketch, "E406", {"start": v(31.46, -7.93) * mm, "end": v(29.46, -4.46) * mm});
            skLineSegment(sketch, "E407", {"start": v(29.46, -4.46) * mm, "end": v(25.46, -4.46) * mm});
            skLineSegment(sketch, "E408", {"start": v(25.46, -4.46) * mm, "end": v(23.46, -7.93) * mm});
            skLineSegment(sketch, "E409", {"start": v(23.46, -7.93) * mm, "end": v(25.46, -11.4) * mm});
            skLineSegment(sketch, "E410", {"start": v(25.46, -19.32) * mm, "end": v(29.46, -19.32) * mm});
            skLineSegment(sketch, "E411", {"start": v(29.46, -19.32) * mm, "end": v(31.46, -15.86) * mm});
            skLineSegment(sketch, "E412", {"start": v(31.46, -15.86) * mm, "end": v(29.46, -12.4) * mm});
            skLineSegment(sketch, "E413", {"start": v(29.46, -12.4) * mm, "end": v(25.46, -12.4) * mm});
            skLineSegment(sketch, "E414", {"start": v(25.46, -12.4) * mm, "end": v(23.46, -15.86) * mm});
            skLineSegment(sketch, "E415", {"start": v(23.46, -15.86) * mm, "end": v(25.46, -19.32) * mm});
            skLineSegment(sketch, "E416", {"start": v(25.46, -27.25) * mm, "end": v(29.46, -27.25) * mm});
            skLineSegment(sketch, "E417", {"start": v(29.46, -27.25) * mm, "end": v(31.46, -23.78) * mm});
            skLineSegment(sketch, "E418", {"start": v(31.46, -23.78) * mm, "end": v(29.46, -20.32) * mm});
            skLineSegment(sketch, "E419", {"start": v(29.46, -20.32) * mm, "end": v(25.46, -20.32) * mm});
            skLineSegment(sketch, "E420", {"start": v(25.46, -20.32) * mm, "end": v(23.46, -23.78) * mm});
            skLineSegment(sketch, "E421", {"start": v(23.46, -23.78) * mm, "end": v(25.46, -27.25) * mm});
            skLineSegment(sketch, "E422", {"start": v(25.46, -35.18) * mm, "end": v(29.46, -35.18) * mm});
            skLineSegment(sketch, "E423", {"start": v(29.46, -35.18) * mm, "end": v(31.46, -31.71) * mm});
            skLineSegment(sketch, "E424", {"start": v(31.46, -31.71) * mm, "end": v(29.46, -28.25) * mm});
            skLineSegment(sketch, "E425", {"start": v(29.46, -28.25) * mm, "end": v(25.46, -28.25) * mm});
            skLineSegment(sketch, "E426", {"start": v(25.46, -28.25) * mm, "end": v(23.46, -31.71) * mm});
            skLineSegment(sketch, "E427", {"start": v(23.46, -31.71) * mm, "end": v(25.46, -35.18) * mm});
            skLineSegment(sketch, "E428", {"start": v(29.46, -36.18) * mm, "end": v(25.46, -36.18) * mm});
            skLineSegment(sketch, "E429", {"start": v(32.33, -7.43) * mm, "end": v(36.33, -7.43) * mm});
            skLineSegment(sketch, "E430", {"start": v(36.33, -0.5) * mm, "end": v(32.33, -0.5) * mm});
            skLineSegment(sketch, "E431", {"start": v(32.33, -0.5) * mm, "end": v(30.33, -3.96) * mm});
            skLineSegment(sketch, "E432", {"start": v(30.33, -3.96) * mm, "end": v(32.33, -7.43) * mm});
            skLineSegment(sketch, "E433", {"start": v(29.46, -4.46) * mm, "end": v(31.46, -7.93) * mm});
            skLineSegment(sketch, "E434", {"start": v(32.33, 0.5) * mm, "end": v(36.33, 0.5) * mm});
            skLineSegment(sketch, "E435", {"start": v(36.33, 7.43) * mm, "end": v(32.33, 7.43) * mm});
            skLineSegment(sketch, "E436", {"start": v(32.33, 7.43) * mm, "end": v(30.33, 3.96) * mm});
            skLineSegment(sketch, "E437", {"start": v(30.33, 3.96) * mm, "end": v(32.33, 0.5) * mm});
            skLineSegment(sketch, "E438", {"start": v(32.33, 8.43) * mm, "end": v(36.33, 8.43) * mm});
            skLineSegment(sketch, "E439", {"start": v(36.33, 15.36) * mm, "end": v(32.33, 15.36) * mm});
            skLineSegment(sketch, "E440", {"start": v(32.33, 15.36) * mm, "end": v(30.33, 11.9) * mm});
            skLineSegment(sketch, "E441", {"start": v(30.33, 11.9) * mm, "end": v(32.33, 8.43) * mm});
            skLineSegment(sketch, "E442", {"start": v(32.33, 16.36) * mm, "end": v(36.33, 16.36) * mm});
            skLineSegment(sketch, "E443", {"start": v(36.33, 23.28) * mm, "end": v(32.33, 23.28) * mm});
            skLineSegment(sketch, "E444", {"start": v(32.33, 23.28) * mm, "end": v(30.33, 19.82) * mm});
            skLineSegment(sketch, "E445", {"start": v(30.33, 19.82) * mm, "end": v(32.33, 16.36) * mm});
            skLineSegment(sketch, "E446", {"start": v(32.33, 24.28) * mm, "end": v(36.33, 24.28) * mm});
            skLineSegment(sketch, "E447", {"start": v(36.33, 31.21) * mm, "end": v(32.33, 31.21) * mm});
            skLineSegment(sketch, "E448", {"start": v(32.33, 31.21) * mm, "end": v(30.33, 27.75) * mm});
            skLineSegment(sketch, "E449", {"start": v(30.33, 27.75) * mm, "end": v(32.33, 24.28) * mm});
            skLineSegment(sketch, "E450", {"start": v(30.33, 35.68) * mm, "end": v(32.33, 32.21) * mm});
            skLineSegment(sketch, "E451", {"start": v(32.33, -15.36) * mm, "end": v(36.33, -15.36) * mm});
            skLineSegment(sketch, "E452", {"start": v(36.33, -8.43) * mm, "end": v(32.33, -8.43) * mm});
            skLineSegment(sketch, "E453", {"start": v(32.33, -8.43) * mm, "end": v(30.33, -11.9) * mm});
            skLineSegment(sketch, "E454", {"start": v(30.33, -11.9) * mm, "end": v(32.33, -15.36) * mm});
            skLineSegment(sketch, "E455", {"start": v(32.33, -23.28) * mm, "end": v(36.33, -23.28) * mm});
            skLineSegment(sketch, "E456", {"start": v(36.33, -16.36) * mm, "end": v(32.33, -16.36) * mm});
            skLineSegment(sketch, "E457", {"start": v(32.33, -16.36) * mm, "end": v(30.33, -19.82) * mm});
            skLineSegment(sketch, "E458", {"start": v(30.33, -19.82) * mm, "end": v(32.33, -23.28) * mm});
            skLineSegment(sketch, "E459", {"start": v(32.33, -31.21) * mm, "end": v(36.33, -31.21) * mm});
            skLineSegment(sketch, "E460", {"start": v(36.33, -24.28) * mm, "end": v(32.33, -24.28) * mm});
            skLineSegment(sketch, "E461", {"start": v(32.33, -24.28) * mm, "end": v(30.33, -27.75) * mm});
            skLineSegment(sketch, "E462", {"start": v(30.33, -27.75) * mm, "end": v(32.33, -31.21) * mm});
            skLineSegment(sketch, "E463", {"start": v(32.33, -32.21) * mm, "end": v(30.33, -35.68) * mm});
            skLineSegment(sketch, "E464", {"start": v(11.73, -3.46) * mm, "end": v(15.73, -3.46) * mm});
            skLineSegment(sketch, "E465", {"start": v(15.73, -3.46) * mm, "end": v(17.73, 0) * mm});
            skLineSegment(sketch, "E466", {"start": v(17.73, 0) * mm, "end": v(15.73, 3.46) * mm});
            skLineSegment(sketch, "E467", {"start": v(15.73, 3.46) * mm, "end": v(11.73, 3.46) * mm});
            skLineSegment(sketch, "E468", {"start": v(11.73, 3.46) * mm, "end": v(9.73, 0) * mm});
            skLineSegment(sketch, "E469", {"start": v(9.73, 0) * mm, "end": v(11.73, -3.46) * mm});
            skLineSegment(sketch, "E470", {"start": v(11.73, 4.46) * mm, "end": v(15.73, 4.46) * mm});
            skLineSegment(sketch, "E471", {"start": v(15.73, 4.46) * mm, "end": v(17.73, 7.93) * mm});
            skLineSegment(sketch, "E472", {"start": v(17.73, 7.93) * mm, "end": v(15.73, 11.4) * mm});
            skLineSegment(sketch, "E473", {"start": v(15.73, 11.4) * mm, "end": v(11.73, 11.4) * mm});
            skLineSegment(sketch, "E474", {"start": v(11.73, 11.4) * mm, "end": v(9.73, 7.93) * mm});
            skLineSegment(sketch, "E475", {"start": v(9.73, 7.93) * mm, "end": v(11.73, 4.46) * mm});
            skLineSegment(sketch, "E476", {"start": v(11.73, 12.4) * mm, "end": v(15.73, 12.4) * mm});
            skLineSegment(sketch, "E477", {"start": v(15.73, 12.4) * mm, "end": v(17.73, 15.86) * mm});
            skLineSegment(sketch, "E478", {"start": v(17.73, 15.86) * mm, "end": v(15.73, 19.32) * mm});
            skLineSegment(sketch, "E479", {"start": v(15.73, 19.32) * mm, "end": v(11.73, 19.32) * mm});
            skLineSegment(sketch, "E480", {"start": v(11.73, 19.32) * mm, "end": v(9.73, 15.86) * mm});
            skLineSegment(sketch, "E481", {"start": v(9.73, 15.86) * mm, "end": v(11.73, 12.4) * mm});
            skLineSegment(sketch, "E482", {"start": v(11.73, 20.32) * mm, "end": v(15.73, 20.32) * mm});
            skLineSegment(sketch, "E483", {"start": v(15.73, 20.32) * mm, "end": v(17.73, 23.78) * mm});
            skLineSegment(sketch, "E484", {"start": v(17.73, 23.78) * mm, "end": v(15.73, 27.25) * mm});
            skLineSegment(sketch, "E485", {"start": v(15.73, 27.25) * mm, "end": v(11.73, 27.25) * mm});
            skLineSegment(sketch, "E486", {"start": v(11.73, 27.25) * mm, "end": v(9.73, 23.78) * mm});
            skLineSegment(sketch, "E487", {"start": v(9.73, 23.78) * mm, "end": v(11.73, 20.32) * mm});
            skLineSegment(sketch, "E488", {"start": v(11.73, 28.25) * mm, "end": v(15.73, 28.25) * mm});
            skLineSegment(sketch, "E489", {"start": v(15.73, 28.25) * mm, "end": v(17.73, 31.71) * mm});
            skLineSegment(sketch, "E490", {"start": v(17.73, 31.71) * mm, "end": v(15.73, 35.18) * mm});
            skLineSegment(sketch, "E491", {"start": v(15.73, 35.18) * mm, "end": v(11.73, 35.18) * mm});
            skLineSegment(sketch, "E492", {"start": v(11.73, 35.18) * mm, "end": v(9.73, 31.71) * mm});
            skLineSegment(sketch, "E493", {"start": v(9.73, 31.71) * mm, "end": v(11.73, 28.25) * mm});
            skLineSegment(sketch, "E494", {"start": v(11.73, 36.18) * mm, "end": v(15.73, 36.18) * mm});
            skLineSegment(sketch, "E495", {"start": v(11.73, -11.4) * mm, "end": v(15.73, -11.4) * mm});
            skLineSegment(sketch, "E496", {"start": v(15.73, -11.4) * mm, "end": v(17.73, -7.93) * mm});
            skLineSegment(sketch, "E497", {"start": v(17.73, -7.93) * mm, "end": v(15.73, -4.46) * mm});
            skLineSegment(sketch, "E498", {"start": v(15.73, -4.46) * mm, "end": v(11.73, -4.46) * mm});
            skLineSegment(sketch, "E499", {"start": v(11.73, -4.46) * mm, "end": v(9.73, -7.93) * mm});
            skLineSegment(sketch, "E500", {"start": v(9.73, -7.93) * mm, "end": v(11.73, -11.4) * mm});
            skLineSegment(sketch, "E501", {"start": v(11.73, -19.32) * mm, "end": v(15.73, -19.32) * mm});
            skLineSegment(sketch, "E502", {"start": v(15.73, -19.32) * mm, "end": v(17.73, -15.86) * mm});
            skLineSegment(sketch, "E503", {"start": v(17.73, -15.86) * mm, "end": v(15.73, -12.4) * mm});
            skLineSegment(sketch, "E504", {"start": v(15.73, -12.4) * mm, "end": v(11.73, -12.4) * mm});
            skLineSegment(sketch, "E505", {"start": v(11.73, -12.4) * mm, "end": v(9.73, -15.86) * mm});
            skLineSegment(sketch, "E506", {"start": v(9.73, -15.86) * mm, "end": v(11.73, -19.32) * mm});
            skLineSegment(sketch, "E507", {"start": v(11.73, -27.25) * mm, "end": v(15.73, -27.25) * mm});
            skLineSegment(sketch, "E508", {"start": v(15.73, -27.25) * mm, "end": v(17.73, -23.78) * mm});
            skLineSegment(sketch, "E509", {"start": v(17.73, -23.78) * mm, "end": v(15.73, -20.32) * mm});
            skLineSegment(sketch, "E510", {"start": v(15.73, -20.32) * mm, "end": v(11.73, -20.32) * mm});
            skLineSegment(sketch, "E511", {"start": v(11.73, -20.32) * mm, "end": v(9.73, -23.78) * mm});
            skLineSegment(sketch, "E512", {"start": v(9.73, -23.78) * mm, "end": v(11.73, -27.25) * mm});
            skLineSegment(sketch, "E513", {"start": v(11.73, -35.18) * mm, "end": v(15.73, -35.18) * mm});
            skLineSegment(sketch, "E514", {"start": v(15.73, -35.18) * mm, "end": v(17.73, -31.71) * mm});
            skLineSegment(sketch, "E515", {"start": v(17.73, -31.71) * mm, "end": v(15.73, -28.25) * mm});
            skLineSegment(sketch, "E516", {"start": v(15.73, -28.25) * mm, "end": v(11.73, -28.25) * mm});
            skLineSegment(sketch, "E517", {"start": v(11.73, -28.25) * mm, "end": v(9.73, -31.71) * mm});
            skLineSegment(sketch, "E518", {"start": v(9.73, -31.71) * mm, "end": v(11.73, -35.18) * mm});
            skLineSegment(sketch, "E519", {"start": v(15.73, -36.18) * mm, "end": v(11.73, -36.18) * mm});
            skLineSegment(sketch, "E520", {"start": v(18.6, -7.43) * mm, "end": v(22.6, -7.43) * mm});
            skLineSegment(sketch, "E521", {"start": v(22.6, -7.43) * mm, "end": v(24.6, -3.96) * mm});
            skLineSegment(sketch, "E522", {"start": v(22.6, -0.5) * mm, "end": v(18.6, -0.5) * mm});
            skLineSegment(sketch, "E523", {"start": v(18.6, -0.5) * mm, "end": v(16.6, -3.96) * mm});
            skLineSegment(sketch, "E524", {"start": v(16.6, -3.96) * mm, "end": v(18.6, -7.43) * mm});
            skLineSegment(sketch, "E525", {"start": v(17.73, 0) * mm, "end": v(15.73, -3.46) * mm});
            skLineSegment(sketch, "E526", {"start": v(15.73, -4.46) * mm, "end": v(17.73, -7.93) * mm});
            skLineSegment(sketch, "E527", {"start": v(18.6, 0.5) * mm, "end": v(22.6, 0.5) * mm});
            skLineSegment(sketch, "E528", {"start": v(24.6, 3.96) * mm, "end": v(22.6, 7.43) * mm});
            skLineSegment(sketch, "E529", {"start": v(22.6, 7.43) * mm, "end": v(18.6, 7.43) * mm});
            skLineSegment(sketch, "E530", {"start": v(18.6, 7.43) * mm, "end": v(16.6, 3.96) * mm});
            skLineSegment(sketch, "E531", {"start": v(16.6, 3.96) * mm, "end": v(18.6, 0.5) * mm});
            skLineSegment(sketch, "E532", {"start": v(18.6, 8.43) * mm, "end": v(22.6, 8.43) * mm});
            skLineSegment(sketch, "E533", {"start": v(22.6, 8.43) * mm, "end": v(24.6, 11.9) * mm});
            skLineSegment(sketch, "E534", {"start": v(24.6, 11.9) * mm, "end": v(22.6, 15.36) * mm});
            skLineSegment(sketch, "E535", {"start": v(22.6, 15.36) * mm, "end": v(18.6, 15.36) * mm});
            skLineSegment(sketch, "E536", {"start": v(18.6, 15.36) * mm, "end": v(16.6, 11.9) * mm});
            skLineSegment(sketch, "E537", {"start": v(16.6, 11.9) * mm, "end": v(18.6, 8.43) * mm});
            skLineSegment(sketch, "E538", {"start": v(18.6, 16.36) * mm, "end": v(22.6, 16.36) * mm});
            skLineSegment(sketch, "E539", {"start": v(22.6, 16.36) * mm, "end": v(24.6, 19.82) * mm});
            skLineSegment(sketch, "E540", {"start": v(24.6, 19.82) * mm, "end": v(22.6, 23.28) * mm});
            skLineSegment(sketch, "E541", {"start": v(22.6, 23.28) * mm, "end": v(18.6, 23.28) * mm});
            skLineSegment(sketch, "E542", {"start": v(18.6, 23.28) * mm, "end": v(16.6, 19.82) * mm});
            skLineSegment(sketch, "E543", {"start": v(16.6, 19.82) * mm, "end": v(18.6, 16.36) * mm});
            skLineSegment(sketch, "E544", {"start": v(18.6, 24.28) * mm, "end": v(22.6, 24.28) * mm});
            skLineSegment(sketch, "E545", {"start": v(22.6, 24.28) * mm, "end": v(24.6, 27.75) * mm});
            skLineSegment(sketch, "E546", {"start": v(24.6, 27.75) * mm, "end": v(22.6, 31.21) * mm});
            skLineSegment(sketch, "E547", {"start": v(22.6, 31.21) * mm, "end": v(18.6, 31.21) * mm});
            skLineSegment(sketch, "E548", {"start": v(18.6, 31.21) * mm, "end": v(16.6, 27.75) * mm});
            skLineSegment(sketch, "E549", {"start": v(16.6, 27.75) * mm, "end": v(18.6, 24.28) * mm});
            skLineSegment(sketch, "E550", {"start": v(18.6, 32.21) * mm, "end": v(22.6, 32.21) * mm});
            skLineSegment(sketch, "E551", {"start": v(22.6, 32.21) * mm, "end": v(24.6, 35.68) * mm});
            skLineSegment(sketch, "E552", {"start": v(16.6, 35.68) * mm, "end": v(18.6, 32.21) * mm});
            skLineSegment(sketch, "E553", {"start": v(18.6, -15.36) * mm, "end": v(22.6, -15.36) * mm});
            skLineSegment(sketch, "E554", {"start": v(22.6, -15.36) * mm, "end": v(24.6, -11.9) * mm});
            skLineSegment(sketch, "E555", {"start": v(24.6, -11.9) * mm, "end": v(22.6, -8.43) * mm});
            skLineSegment(sketch, "E556", {"start": v(22.6, -8.43) * mm, "end": v(18.6, -8.43) * mm});
            skLineSegment(sketch, "E557", {"start": v(18.6, -8.43) * mm, "end": v(16.6, -11.9) * mm});
            skLineSegment(sketch, "E558", {"start": v(16.6, -11.9) * mm, "end": v(18.6, -15.36) * mm});
            skLineSegment(sketch, "E559", {"start": v(18.6, -23.28) * mm, "end": v(22.6, -23.28) * mm});
            skLineSegment(sketch, "E560", {"start": v(22.6, -23.28) * mm, "end": v(24.6, -19.82) * mm});
            skLineSegment(sketch, "E561", {"start": v(24.6, -19.82) * mm, "end": v(22.6, -16.36) * mm});
            skLineSegment(sketch, "E562", {"start": v(22.6, -16.36) * mm, "end": v(18.6, -16.36) * mm});
            skLineSegment(sketch, "E563", {"start": v(18.6, -16.36) * mm, "end": v(16.6, -19.82) * mm});
            skLineSegment(sketch, "E564", {"start": v(16.6, -19.82) * mm, "end": v(18.6, -23.28) * mm});
            skLineSegment(sketch, "E565", {"start": v(18.6, -31.21) * mm, "end": v(22.6, -31.21) * mm});
            skLineSegment(sketch, "E566", {"start": v(22.6, -31.21) * mm, "end": v(24.6, -27.75) * mm});
            skLineSegment(sketch, "E567", {"start": v(24.6, -27.75) * mm, "end": v(22.6, -24.28) * mm});
            skLineSegment(sketch, "E568", {"start": v(22.6, -24.28) * mm, "end": v(18.6, -24.28) * mm});
            skLineSegment(sketch, "E569", {"start": v(18.6, -24.28) * mm, "end": v(16.6, -27.75) * mm});
            skLineSegment(sketch, "E570", {"start": v(16.6, -27.75) * mm, "end": v(18.6, -31.21) * mm});
            skLineSegment(sketch, "E571", {"start": v(24.6, -35.68) * mm, "end": v(22.6, -32.21) * mm});
            skLineSegment(sketch, "E572", {"start": v(22.6, -32.21) * mm, "end": v(18.6, -32.21) * mm});
            skLineSegment(sketch, "E573", {"start": v(18.6, -32.21) * mm, "end": v(16.6, -35.68) * mm});
            skCircle(sketch, "E574", {"center": v(-35.75, -35.75) * mm, "radius": 2.25 * mm});
            skCircle(sketch, "E575", {"center": v(35.75, -35.75) * mm, "radius": 2.25 * mm});
            skCircle(sketch, "E576", {"center": v(-35.75, 35.75) * mm, "radius": 2.25 * mm});
            skCircle(sketch, "E577", {"center": v(35.75, 35.75) * mm, "radius": 2.25 * mm});
            skArc(sketch, "E578", {"start": v(40, 35.85) * mm, "mid": v(38.78, 38.78) * mm, "end": v(35.85, 40) * mm});
            skLineSegment(sketch, "E579", {"start": v(35.85, 40) * mm, "end": v(-35.85, 40) * mm});
            skArc(sketch, "E580", {"start": v(-35.85, 40) * mm, "mid": v(-38.78, 38.78) * mm, "end": v(-40, 35.85) * mm});
            skLineSegment(sketch, "E581", {"start": v(-40, 35.85) * mm, "end": v(-40, -35.85) * mm});
            skArc(sketch, "E582", {"start": v(-40, -35.85) * mm, "mid": v(-38.78, -38.78) * mm, "end": v(-35.85, -40) * mm});
            skLineSegment(sketch, "E583", {"start": v(40, -35.85) * mm, "end": v(40, 35.85) * mm});
            skLineSegment(sketch, "E584", {"start": v(-35.85, -40) * mm, "end": v(35.85, -40) * mm});
            skArc(sketch, "E585", {"start": v(35.85, -40) * mm, "mid": v(38.78, -38.78) * mm, "end": v(40, -35.85) * mm});
            skArc(sketch, "E586", {"start": v(-29.5, 38) * mm, "mid": v(-29.96, 37.95) * mm, "end": v(-30.4, 37.8) * mm});
            skArc(sketch, "E587", {"start": v(-33.4, 32.21) * mm, "mid": v(-31.96, 33.82) * mm, "end": v(-31.5, 35.92) * mm});
            skLineSegment(sketch, "E588", {"start": v(29.5, 38) * mm, "end": v(24.41, 38) * mm});
            skArc(sketch, "E589", {"start": v(31.5, 35.92) * mm, "mid": v(31.43, 36.55) * mm, "end": v(31.16, 37.12) * mm});
            skArc(sketch, "E590", {"start": v(31.5, 35.92) * mm, "mid": v(31.96, 33.82) * mm, "end": v(33.4, 32.21) * mm});
            skLineSegment(sketch, "E591", {"start": v(38, -28.32) * mm, "end": v(38, -27.18) * mm});
            skArc(sketch, "E592", {"start": v(33.4, -32.21) * mm, "mid": v(31.96, -33.82) * mm, "end": v(31.5, -35.92) * mm});
            skArc(sketch, "E593", {"start": v(29.5, -38) * mm, "mid": v(29.96, -37.95) * mm, "end": v(30.4, -37.8) * mm});
            skLineSegment(sketch, "E594", {"start": v(-29.5, -38) * mm, "end": v(-24.41, -38) * mm});
            skArc(sketch, "E595", {"start": v(-31.5, -35.92) * mm, "mid": v(-31.43, -36.55) * mm, "end": v(-31.16, -37.12) * mm});
            skArc(sketch, "E596", {"start": v(-31.5, -35.92) * mm, "mid": v(-31.96, -33.82) * mm, "end": v(-33.4, -32.21) * mm});
            skLineSegment(sketch, "E597", {"start": v(-38, 28.32) * mm, "end": v(-38, 27.18) * mm});
            skLineSegment(sketch, "E598", {"start": v(-25.46, 36.18) * mm, "end": v(-24.41, 38) * mm});
            skLineSegment(sketch, "E599", {"start": v(-23.26, 38) * mm, "end": v(-24.6, 35.68) * mm});
            skLineSegment(sketch, "E600", {"start": v(-16.6, 35.68) * mm, "end": v(-17.94, 38) * mm});
            skLineSegment(sketch, "E601", {"start": v(-16.78, 38) * mm, "end": v(-15.73, 36.18) * mm});
            skLineSegment(sketch, "E602", {"start": v(-11.73, 36.18) * mm, "end": v(-10.68, 38) * mm});
            skLineSegment(sketch, "E603", {"start": v(-9.52, 38) * mm, "end": v(-10.87, 35.68) * mm});
            skLineSegment(sketch, "E604", {"start": v(-3.05, 38) * mm, "end": v(-2, 36.18) * mm});
            skLineSegment(sketch, "E605", {"start": v(-2.87, 35.68) * mm, "end": v(-4.2, 38) * mm});
            skLineSegment(sketch, "E606", {"start": v(2, 36.18) * mm, "end": v(3.05, 38) * mm});
            skLineSegment(sketch, "E607", {"start": v(4.2, 38) * mm, "end": v(2.87, 35.68) * mm});
            skLineSegment(sketch, "E608", {"start": v(10.87, 35.68) * mm, "end": v(9.52, 38) * mm});
            skLineSegment(sketch, "E609", {"start": v(10.68, 38) * mm, "end": v(11.73, 36.18) * mm});
            skLineSegment(sketch, "E610", {"start": v(17.94, 38) * mm, "end": v(16.6, 35.68) * mm});
            skLineSegment(sketch, "E611", {"start": v(15.73, 36.18) * mm, "end": v(16.78, 38) * mm});
            skLineSegment(sketch, "E612", {"start": v(24.6, 35.68) * mm, "end": v(23.26, 38) * mm});
            skLineSegment(sketch, "E613", {"start": v(24.41, 38) * mm, "end": v(25.46, 36.18) * mm});
            skLineSegment(sketch, "E614", {"start": v(38, 28.32) * mm, "end": v(36.33, 31.21) * mm});
            skLineSegment(sketch, "E615", {"start": v(36.33, 24.28) * mm, "end": v(38, 27.18) * mm});
            skLineSegment(sketch, "E616", {"start": v(38, 25.18) * mm, "end": v(37.2, 23.78) * mm});
            skLineSegment(sketch, "E617", {"start": v(37.2, 23.78) * mm, "end": v(38, 22.4) * mm});
            skLineSegment(sketch, "E618", {"start": v(38, 20.4) * mm, "end": v(36.33, 23.28) * mm});
            skLineSegment(sketch, "E619", {"start": v(36.33, 16.36) * mm, "end": v(38, 19.25) * mm});
            skLineSegment(sketch, "E620", {"start": v(38, 17.25) * mm, "end": v(37.2, 15.86) * mm});
            skLineSegment(sketch, "E621", {"start": v(37.2, 15.86) * mm, "end": v(38, 14.46) * mm});
            skLineSegment(sketch, "E622", {"start": v(38, 12.46) * mm, "end": v(36.33, 15.36) * mm});
            skLineSegment(sketch, "E623", {"start": v(36.33, 8.43) * mm, "end": v(38, 11.32) * mm});
            skLineSegment(sketch, "E624", {"start": v(38, 9.32) * mm, "end": v(37.2, 7.93) * mm});
            skLineSegment(sketch, "E625", {"start": v(37.2, 7.93) * mm, "end": v(38, 6.54) * mm});
            skLineSegment(sketch, "E626", {"start": v(38, 4.54) * mm, "end": v(36.33, 7.43) * mm});
            skLineSegment(sketch, "E627", {"start": v(36.33, 0.5) * mm, "end": v(38, 3.4) * mm});
            skLineSegment(sketch, "E628", {"start": v(38, 1.4) * mm, "end": v(37.2, 0) * mm});
            skLineSegment(sketch, "E629", {"start": v(37.2, 0) * mm, "end": v(38, -1.4) * mm});
            skLineSegment(sketch, "E630", {"start": v(38, -3.4) * mm, "end": v(36.33, -0.5) * mm});
            skLineSegment(sketch, "E631", {"start": v(36.33, -7.43) * mm, "end": v(38, -4.54) * mm});
            skLineSegment(sketch, "E632", {"start": v(38, -6.54) * mm, "end": v(37.2, -7.93) * mm});
            skLineSegment(sketch, "E633", {"start": v(38, -11.32) * mm, "end": v(36.33, -8.43) * mm});
            skLineSegment(sketch, "E634", {"start": v(37.2, -7.93) * mm, "end": v(38, -9.32) * mm});
            skLineSegment(sketch, "E635", {"start": v(36.33, -15.36) * mm, "end": v(38, -12.46) * mm});
            skLineSegment(sketch, "E636", {"start": v(38, -14.46) * mm, "end": v(37.2, -15.86) * mm});
            skLineSegment(sketch, "E637", {"start": v(37.2, -15.86) * mm, "end": v(38, -17.25) * mm});
            skLineSegment(sketch, "E638", {"start": v(38, -19.25) * mm, "end": v(36.33, -16.36) * mm});
            skLineSegment(sketch, "E639", {"start": v(36.33, -23.28) * mm, "end": v(38, -20.4) * mm});
            skLineSegment(sketch, "E640", {"start": v(38, -22.4) * mm, "end": v(37.2, -23.78) * mm});
            skLineSegment(sketch, "E641", {"start": v(37.2, -23.78) * mm, "end": v(38, -25.18) * mm});
            skLineSegment(sketch, "E642", {"start": v(38, -27.18) * mm, "end": v(36.33, -24.28) * mm});
            skLineSegment(sketch, "E643", {"start": v(36.33, -31.21) * mm, "end": v(38, -28.32) * mm});
            skLineSegment(sketch, "E644", {"start": v(25.46, -36.18) * mm, "end": v(24.41, -38) * mm});
            skLineSegment(sketch, "E645", {"start": v(23.26, -38) * mm, "end": v(24.6, -35.68) * mm});
            skLineSegment(sketch, "E646", {"start": v(16.6, -35.68) * mm, "end": v(17.94, -38) * mm});
            skLineSegment(sketch, "E647", {"start": v(16.78, -38) * mm, "end": v(15.73, -36.18) * mm});
            skLineSegment(sketch, "E648", {"start": v(11.73, -36.18) * mm, "end": v(10.68, -38) * mm});
            skLineSegment(sketch, "E649", {"start": v(9.52, -38) * mm, "end": v(10.87, -35.68) * mm});
            skLineSegment(sketch, "E650", {"start": v(2.87, -35.68) * mm, "end": v(4.2, -38) * mm});
            skLineSegment(sketch, "E651", {"start": v(3.05, -38) * mm, "end": v(2, -36.18) * mm});
            skLineSegment(sketch, "E652", {"start": v(-2, -36.18) * mm, "end": v(-3.05, -38) * mm});
            skLineSegment(sketch, "E653", {"start": v(-4.2, -38) * mm, "end": v(-2.87, -35.68) * mm});
            skLineSegment(sketch, "E654", {"start": v(-10.87, -35.68) * mm, "end": v(-9.52, -38) * mm});
            skLineSegment(sketch, "E655", {"start": v(-10.68, -38) * mm, "end": v(-11.73, -36.18) * mm});
            skLineSegment(sketch, "E656", {"start": v(-17.94, -38) * mm, "end": v(-16.6, -35.68) * mm});
            skLineSegment(sketch, "E657", {"start": v(-15.73, -36.18) * mm, "end": v(-16.78, -38) * mm});
            skLineSegment(sketch, "E658", {"start": v(-24.41, -38) * mm, "end": v(-25.46, -36.18) * mm});
            skLineSegment(sketch, "E659", {"start": v(-24.6, -35.68) * mm, "end": v(-23.26, -38) * mm});
            skLineSegment(sketch, "E660", {"start": v(-38, -28.32) * mm, "end": v(-36.33, -31.21) * mm});
            skLineSegment(sketch, "E661", {"start": v(-36.33, -24.28) * mm, "end": v(-38, -27.18) * mm});
            skLineSegment(sketch, "E662", {"start": v(-38, -25.18) * mm, "end": v(-37.2, -23.78) * mm});
            skLineSegment(sketch, "E663", {"start": v(-37.2, -23.78) * mm, "end": v(-38, -22.4) * mm});
            skLineSegment(sketch, "E664", {"start": v(-38, -20.4) * mm, "end": v(-36.33, -23.28) * mm});
            skLineSegment(sketch, "E665", {"start": v(-36.33, -16.36) * mm, "end": v(-38, -19.25) * mm});
            skLineSegment(sketch, "E666", {"start": v(-38, -17.25) * mm, "end": v(-37.2, -15.86) * mm});
            skLineSegment(sketch, "E667", {"start": v(-37.2, -15.86) * mm, "end": v(-38, -14.46) * mm});
            skLineSegment(sketch, "E668", {"start": v(-38, -12.46) * mm, "end": v(-36.33, -15.36) * mm});
            skLineSegment(sketch, "E669", {"start": v(-36.33, -8.43) * mm, "end": v(-38, -11.32) * mm});
            skLineSegment(sketch, "E670", {"start": v(-38, -9.32) * mm, "end": v(-37.2, -7.93) * mm});
            skLineSegment(sketch, "E671", {"start": v(-38, -6.54) * mm, "end": v(-37.2, -7.93) * mm});
            skLineSegment(sketch, "E672", {"start": v(-38, -4.54) * mm, "end": v(-36.33, -7.43) * mm});
            skLineSegment(sketch, "E673", {"start": v(-37.2, -7.93) * mm, "end": v(-38, -6.54) * mm});
            skLineSegment(sketch, "E674", {"start": v(-38, -1.4) * mm, "end": v(-37.2, 0) * mm});
            skLineSegment(sketch, "E675", {"start": v(-37.2, 0) * mm, "end": v(-38, -1.4) * mm});
            skLineSegment(sketch, "E676", {"start": v(-36.33, -0.5) * mm, "end": v(-38, -3.4) * mm});
            skLineSegment(sketch, "E677", {"start": v(-37.2, 0) * mm, "end": v(-38, 1.4) * mm});
            skLineSegment(sketch, "E678", {"start": v(-38, 3.4) * mm, "end": v(-36.33, 0.5) * mm});
            skLineSegment(sketch, "E679", {"start": v(-36.33, 7.43) * mm, "end": v(-38, 4.54) * mm});
            skLineSegment(sketch, "E680", {"start": v(-37.2, 7.93) * mm, "end": v(-38, 9.32) * mm});
            skLineSegment(sketch, "E681", {"start": v(-38, 6.54) * mm, "end": v(-37.2, 7.93) * mm});
            skLineSegment(sketch, "E682", {"start": v(-38, 11.32) * mm, "end": v(-36.33, 8.43) * mm});
            skLineSegment(sketch, "E683", {"start": v(-36.33, 15.36) * mm, "end": v(-38, 12.46) * mm});
            skLineSegment(sketch, "E684", {"start": v(-38, 14.46) * mm, "end": v(-37.2, 15.86) * mm});
            skLineSegment(sketch, "E685", {"start": v(-37.2, 15.86) * mm, "end": v(-38, 17.25) * mm});
            skLineSegment(sketch, "E686", {"start": v(-38, 19.25) * mm, "end": v(-36.33, 16.36) * mm});
            skLineSegment(sketch, "E687", {"start": v(-36.33, 23.28) * mm, "end": v(-38, 20.4) * mm});
            skLineSegment(sketch, "E688", {"start": v(-38, 22.4) * mm, "end": v(-37.2, 23.78) * mm});
            skLineSegment(sketch, "E689", {"start": v(-37.2, 23.78) * mm, "end": v(-38, 25.18) * mm});
            skLineSegment(sketch, "E690", {"start": v(-38, 27.18) * mm, "end": v(-36.33, 24.28) * mm});
            skLineSegment(sketch, "E691", {"start": v(-36.33, 31.21) * mm, "end": v(-38, 28.32) * mm});
            skLineSegment(sketch, "E692", {"start": v(-33.4, 32.21) * mm, "end": v(-32.33, 32.21) * mm});
            skLineSegment(sketch, "E693", {"start": v(-30.33, 35.68) * mm, "end": v(-31.16, 37.12) * mm});
            skLineSegment(sketch, "E694", {"start": v(-30.4, 37.8) * mm, "end": v(-29.46, 36.18) * mm});
            skLineSegment(sketch, "E695", {"start": v(-23.26, 38) * mm, "end": v(-17.94, 38) * mm});
            skLineSegment(sketch, "E696", {"start": v(-16.78, 38) * mm, "end": v(-10.68, 38) * mm});
            skLineSegment(sketch, "E697", {"start": v(-9.52, 38) * mm, "end": v(-4.2, 38) * mm});
            skLineSegment(sketch, "E698", {"start": v(-3.05, 38) * mm, "end": v(3.05, 38) * mm});
            skLineSegment(sketch, "E699", {"start": v(4.2, 38) * mm, "end": v(9.52, 38) * mm});
            skLineSegment(sketch, "E700", {"start": v(10.68, 38) * mm, "end": v(16.78, 38) * mm});
            skLineSegment(sketch, "E701", {"start": v(17.94, 38) * mm, "end": v(23.26, 38) * mm});
            skLineSegment(sketch, "E702", {"start": v(-38, 17.25) * mm, "end": v(-38, 14.46) * mm});
            skLineSegment(sketch, "E703", {"start": v(-38, 20.4) * mm, "end": v(-38, 19.25) * mm});
            skLineSegment(sketch, "E704", {"start": v(-38, 12.46) * mm, "end": v(-38, 11.32) * mm});
            skLineSegment(sketch, "E705", {"start": v(-38, 9.32) * mm, "end": v(-38, 6.54) * mm});
            skLineSegment(sketch, "E706", {"start": v(-38, 4.54) * mm, "end": v(-38, 3.4) * mm});
            skLineSegment(sketch, "E707", {"start": v(-38, 1.4) * mm, "end": v(-38, -1.4) * mm});
            skLineSegment(sketch, "E708", {"start": v(-38, -3.4) * mm, "end": v(-38, -4.54) * mm});
            skLineSegment(sketch, "E709", {"start": v(-38, -6.54) * mm, "end": v(-38, -9.32) * mm});
            skLineSegment(sketch, "E710", {"start": v(-38, -11.32) * mm, "end": v(-38, -12.46) * mm});
            skLineSegment(sketch, "E711", {"start": v(-38, -14.46) * mm, "end": v(-38, -17.25) * mm});
            skLineSegment(sketch, "E712", {"start": v(-38, -19.25) * mm, "end": v(-38, -20.4) * mm});
            skLineSegment(sketch, "E713", {"start": v(-38, -22.4) * mm, "end": v(-38, -25.18) * mm});
            skLineSegment(sketch, "E714", {"start": v(-38, -27.18) * mm, "end": v(-38, -28.32) * mm});
            skLineSegment(sketch, "E715", {"start": v(-23.26, -38) * mm, "end": v(-17.94, -38) * mm});
            skLineSegment(sketch, "E716", {"start": v(-16.78, -38) * mm, "end": v(-10.68, -38) * mm});
            skLineSegment(sketch, "E717", {"start": v(-9.52, -38) * mm, "end": v(-4.2, -38) * mm});
            skLineSegment(sketch, "E718", {"start": v(-3.05, -38) * mm, "end": v(3.05, -38) * mm});
            skLineSegment(sketch, "E719", {"start": v(4.2, -38) * mm, "end": v(9.52, -38) * mm});
            skLineSegment(sketch, "E720", {"start": v(10.68, -38) * mm, "end": v(16.78, -38) * mm});
            skLineSegment(sketch, "E721", {"start": v(17.94, -38) * mm, "end": v(23.26, -38) * mm});
            skLineSegment(sketch, "E722", {"start": v(38, 28.32) * mm, "end": v(38, 27.18) * mm});
            skLineSegment(sketch, "E723", {"start": v(38, 25.18) * mm, "end": v(38, 22.4) * mm});
            skLineSegment(sketch, "E724", {"start": v(38, 20.4) * mm, "end": v(38, 19.25) * mm});
            skLineSegment(sketch, "E725", {"start": v(38, 17.25) * mm, "end": v(38, 14.46) * mm});
            skLineSegment(sketch, "E726", {"start": v(38, 12.46) * mm, "end": v(38, 11.32) * mm});
            skLineSegment(sketch, "E727", {"start": v(38, 9.32) * mm, "end": v(38, 6.54) * mm});
            skLineSegment(sketch, "E728", {"start": v(38, 4.54) * mm, "end": v(38, 3.4) * mm});
            skLineSegment(sketch, "E729", {"start": v(38, 1.4) * mm, "end": v(38, -1.4) * mm});
            skLineSegment(sketch, "E730", {"start": v(38, -3.4) * mm, "end": v(38, -4.54) * mm});
            skLineSegment(sketch, "E731", {"start": v(38, -6.54) * mm, "end": v(38, -9.32) * mm});
            skLineSegment(sketch, "E732", {"start": v(38, -11.32) * mm, "end": v(38, -12.46) * mm});
            skLineSegment(sketch, "E733", {"start": v(38, -14.46) * mm, "end": v(38, -17.25) * mm});
            skLineSegment(sketch, "E734", {"start": v(38, -19.25) * mm, "end": v(38, -20.4) * mm});
            skLineSegment(sketch, "E735", {"start": v(38, -22.4) * mm, "end": v(38, -25.18) * mm});
            skLineSegment(sketch, "E736", {"start": v(38, -27.18) * mm, "end": v(38, -28.32) * mm});
            skArc(sketch, "E737", {"start": v(-31.16, 37.12) * mm, "mid": v(-31.43, 36.55) * mm, "end": v(-31.5, 35.92) * mm});
            skLineSegment(sketch, "E738", {"start": v(-29.5, 38) * mm, "end": v(-24.41, 38) * mm});
            skLineSegment(sketch, "E739", {"start": v(24.41, 38) * mm, "end": v(29.5, 38) * mm});
            skArc(sketch, "E740", {"start": v(30.4, 37.8) * mm, "mid": v(29.96, 37.95) * mm, "end": v(29.5, 38) * mm});
            skLineSegment(sketch, "E741", {"start": v(29.46, 36.18) * mm, "end": v(30.4, 37.8) * mm});
            skLineSegment(sketch, "E742", {"start": v(31.16, 37.12) * mm, "end": v(30.33, 35.68) * mm});
            skLineSegment(sketch, "E743", {"start": v(32.33, 32.21) * mm, "end": v(33.4, 32.21) * mm});
            skArc(sketch, "E744", {"start": v(31.16, -37.12) * mm, "mid": v(31.43, -36.55) * mm, "end": v(31.5, -35.92) * mm});
            skLineSegment(sketch, "E745", {"start": v(30.33, -35.68) * mm, "end": v(31.16, -37.12) * mm});
            skLineSegment(sketch, "E746", {"start": v(33.4, -32.21) * mm, "end": v(32.33, -32.21) * mm});
            skLineSegment(sketch, "E747", {"start": v(29.5, -38) * mm, "end": v(24.41, -38) * mm});
            skLineSegment(sketch, "E748", {"start": v(30.4, -37.8) * mm, "end": v(29.46, -36.18) * mm});
            skLineSegment(sketch, "E749", {"start": v(-31.16, -37.12) * mm, "end": v(-30.33, -35.68) * mm});
            skArc(sketch, "E750", {"start": v(-30.4, -37.8) * mm, "mid": v(-29.96, -37.95) * mm, "end": v(-29.5, -38) * mm});
            skLineSegment(sketch, "E751", {"start": v(-29.46, -36.18) * mm, "end": v(-30.4, -37.8) * mm});
            skLineSegment(sketch, "E752", {"start": v(-32.33, -32.21) * mm, "end": v(-33.4, -32.21) * mm});
            skLineSegment(sketch, "E753.trimOffspring", {"start": v(-24.41, 38) * mm, "end": v(-29.5, 38) * mm});
            skLineSegment(sketch, "E754.trimOffspring", {"start": v(-38, 25.18) * mm, "end": v(-38, 22.4) * mm});
            skLineSegment(sketch, "E755.trimOffspring", {"start": v(24.41, -38) * mm, "end": v(29.5, -38) * mm});
            skLineSegment(sketch, "E756.trimOffspring", {"start": v(38, -25.18) * mm, "end": v(38, -22.4) * mm});
            skLineSegment(sketch, "E757.trimOffspring", {"start": v(38, -20.4) * mm, "end": v(38, -19.25) * mm});
            skLineSegment(sketch, "E758.trimOffspring", {"start": v(38, -17.25) * mm, "end": v(38, -14.46) * mm});
            skLineSegment(sketch, "E759.trimOffspring", {"start": v(38, -12.46) * mm, "end": v(38, -11.32) * mm});
            skLineSegment(sketch, "E760.trimOffspring", {"start": v(38, -9.32) * mm, "end": v(38, -6.54) * mm});
            skLineSegment(sketch, "E761.trimOffspring", {"start": v(38, -4.54) * mm, "end": v(38, -3.4) * mm});
            skLineSegment(sketch, "E762.trimOffspring", {"start": v(38, -1.4) * mm, "end": v(38, 1.4) * mm});
            skLineSegment(sketch, "E763.trimOffspring", {"start": v(38, 3.4) * mm, "end": v(38, 4.54) * mm});
            skLineSegment(sketch, "E764.trimOffspring", {"start": v(38, 6.54) * mm, "end": v(38, 9.32) * mm});
            skLineSegment(sketch, "E765.trimOffspring", {"start": v(38, 11.32) * mm, "end": v(38, 12.46) * mm});
            skLineSegment(sketch, "E766.trimOffspring", {"start": v(38, 14.46) * mm, "end": v(38, 17.25) * mm});
            skLineSegment(sketch, "E767.trimOffspring", {"start": v(38, 19.25) * mm, "end": v(38, 20.4) * mm});
            skLineSegment(sketch, "E768.trimOffspring", {"start": v(38, 22.4) * mm, "end": v(38, 25.18) * mm});
            skLineSegment(sketch, "E769.trimOffspring", {"start": v(38, 27.18) * mm, "end": v(38, 28.32) * mm});
            skLineSegment(sketch, "E770.trimOffspring", {"start": v(23.26, 38) * mm, "end": v(17.94, 38) * mm});
            skLineSegment(sketch, "E771.trimOffspring", {"start": v(16.78, 38) * mm, "end": v(10.68, 38) * mm});
            skLineSegment(sketch, "E772.trimOffspring", {"start": v(9.52, 38) * mm, "end": v(4.2, 38) * mm});
            skLineSegment(sketch, "E773.trimOffspring", {"start": v(3.05, 38) * mm, "end": v(-3.05, 38) * mm});
            skLineSegment(sketch, "E774.trimOffspring", {"start": v(-4.2, 38) * mm, "end": v(-9.52, 38) * mm});
            skLineSegment(sketch, "E775.trimOffspring", {"start": v(-10.68, 38) * mm, "end": v(-16.78, 38) * mm});
            skLineSegment(sketch, "E776.trimOffspring", {"start": v(-17.94, 38) * mm, "end": v(-23.26, 38) * mm});
            skSolve(sketch);
        }
        {
            var Q0;
            Q0 = qSketchRegion(id + "F0", true);
            extrude(context, id + "F1", {"entities" : qUnion([Q0]), "depth" : 2.54 * mm, "offsetDistance" : 25.4 * mm});
        }
        {
            var Q0;
            Q0=makeQuery(id+"F1.opExtrude","CAP_FACE",FACE,{"disambiguationData":[OSD([sQuery(id+"F0.wireOp",EDGE,"E2"),sQuery(id+"F0.wireOp",EDGE,"E4"),sQuery(id+"F0.wireOp",EDGE,"E5"),sQuery(id+"F0.wireOp",EDGE,"E6"),sQuery(id+"F0.wireOp",EDGE,"E7"),sQuery(id+"F0.wireOp",EDGE,"E8"),sQuery(id+"F0.wireOp",EDGE,"E9"),sQuery(id+"F0.wireOp",EDGE,"E10"),sQuery(id+"F0.wireOp",EDGE,"E11"),sQuery(id+"F0.wireOp",EDGE,"E12"),sQuery(id+"F0.wireOp",EDGE,"E13"),sQuery(id+"F0.wireOp",EDGE,"E14"),sQuery(id+"F0.wireOp",EDGE,"E15"),sQuery(id+"F0.wireOp",EDGE,"E16"),sQuery(id+"F0.wireOp",EDGE,"E17"),sQuery(id+"F0.wireOp",EDGE,"E18"),sQuery(id+"F0.wireOp",EDGE,"E19"),sQuery(id+"F0.wireOp",EDGE,"E20"),sQuery(id+"F0.wireOp",EDGE,"E21"),sQuery(id+"F0.wireOp",EDGE,"E22"),sQuery(id+"F0.wireOp",EDGE,"E23"),sQuery(id+"F0.wireOp",EDGE,"E24"),sQuery(id+"F0.wireOp",EDGE,"E25"),sQuery(id+"F0.wireOp",EDGE,"E26"),sQuery(id+"F0.wireOp",EDGE,"E27"),sQuery(id+"F0.wireOp",EDGE,"E28"),sQuery(id+"F0.wireOp",EDGE,"E29"),sQuery(id+"F0.wireOp",EDGE,"E30"),sQuery(id+"F0.wireOp",EDGE,"E31"),sQuery(id+"F0.wireOp",EDGE,"E32"),sQuery(id+"F0.wireOp",EDGE,"E33"),sQuery(id+"F0.wireOp",EDGE,"E34"),sQuery(id+"F0.wireOp",EDGE,"E35"),sQuery(id+"F0.wireOp",EDGE,"E36"),sQuery(id+"F0.wireOp",EDGE,"E38"),sQuery(id+"F0.wireOp",EDGE,"E39"),sQuery(id+"F0.wireOp",EDGE,"E40"),sQuery(id+"F0.wireOp",EDGE,"E41"),sQuery(id+"F0.wireOp",EDGE,"E42"),sQuery(id+"F0.wireOp",EDGE,"E43"),sQuery(id+"F0.wireOp",EDGE,"E44"),sQuery(id+"F0.wireOp",EDGE,"E45"),sQuery(id+"F0.wireOp",EDGE,"E46"),sQuery(id+"F0.wireOp",EDGE,"E47"),sQuery(id+"F0.wireOp",EDGE,"E48"),sQuery(id+"F0.wireOp",EDGE,"E49"),sQuery(id+"F0.wireOp",EDGE,"E50"),sQuery(id+"F0.wireOp",EDGE,"E51"),sQuery(id+"F0.wireOp",EDGE,"E52"),sQuery(id+"F0.wireOp",EDGE,"E53"),sQuery(id+"F0.wireOp",EDGE,"E54"),sQuery(id+"F0.wireOp",EDGE,"E55"),sQuery(id+"F0.wireOp",EDGE,"E56"),sQuery(id+"F0.wireOp",EDGE,"E57"),sQuery(id+"F0.wireOp",EDGE,"E58"),sQuery(id+"F0.wireOp",EDGE,"E59"),sQuery(id+"F0.wireOp",EDGE,"E60"),sQuery(id+"F0.wireOp",EDGE,"E61"),sQuery(id+"F0.wireOp",EDGE,"E62"),sQuery(id+"F0.wireOp",EDGE,"E63"),sQuery(id+"F0.wireOp",EDGE,"E64"),sQuery(id+"F0.wireOp",EDGE,"E65"),sQuery(id+"F0.wireOp",EDGE,"E66"),sQuery(id+"F0.wireOp",EDGE,"E67"),sQuery(id+"F0.wireOp",EDGE,"E68"),sQuery(id+"F0.wireOp",EDGE,"E69"),sQuery(id+"F0.wireOp",EDGE,"E70"),sQuery(id+"F0.wireOp",EDGE,"E71"),sQuery(id+"F0.wireOp",EDGE,"E72"),sQuery(id+"F0.wireOp",EDGE,"E73"),sQuery(id+"F0.wireOp",EDGE,"E74"),sQuery(id+"F0.wireOp",EDGE,"E75"),sQuery(id+"F0.wireOp",EDGE,"E76"),sQuery(id+"F0.wireOp",EDGE,"E77"),sQuery(id+"F0.wireOp",EDGE,"E78"),sQuery(id+"F0.wireOp",EDGE,"E79"),sQuery(id+"F0.wireOp",EDGE,"E80"),sQuery(id+"F0.wireOp",EDGE,"E81"),sQuery(id+"F0.wireOp",EDGE,"E82"),sQuery(id+"F0.wireOp",EDGE,"E83"),sQuery(id+"F0.wireOp",EDGE,"E84"),sQuery(id+"F0.wireOp",EDGE,"E85"),sQuery(id+"F0.wireOp",EDGE,"E86"),sQuery(id+"F0.wireOp",EDGE,"E87"),sQuery(id+"F0.wireOp",EDGE,"E88"),sQuery(id+"F0.wireOp",EDGE,"E89"),sQuery(id+"F0.wireOp",EDGE,"E90"),sQuery(id+"F0.wireOp",EDGE,"E91"),sQuery(id+"F0.wireOp",EDGE,"E92"),sQuery(id+"F0.wireOp",EDGE,"E93"),sQuery(id+"F0.wireOp",EDGE,"E94"),sQuery(id+"F0.wireOp",EDGE,"E95"),sQuery(id+"F0.wireOp",EDGE,"E96"),sQuery(id+"F0.wireOp",EDGE,"E97"),sQuery(id+"F0.wireOp",EDGE,"E98"),sQuery(id+"F0.wireOp",EDGE,"E99"),sQuery(id+"F0.wireOp",EDGE,"E100"),sQuery(id+"F0.wireOp",EDGE,"E101"),sQuery(id+"F0.wireOp",EDGE,"E102"),sQuery(id+"F0.wireOp",EDGE,"E103"),sQuery(id+"F0.wireOp",EDGE,"E104"),sQuery(id+"F0.wireOp",EDGE,"E105"),sQuery(id+"F0.wireOp",EDGE,"E106"),sQuery(id+"F0.wireOp",EDGE,"E107"),sQuery(id+"F0.wireOp",EDGE,"E108"),sQuery(id+"F0.wireOp",EDGE,"E109"),sQuery(id+"F0.wireOp",EDGE,"E110"),sQuery(id+"F0.wireOp",EDGE,"E111"),sQuery(id+"F0.wireOp",EDGE,"E112"),sQuery(id+"F0.wireOp",EDGE,"E113"),sQuery(id+"F0.wireOp",EDGE,"E114"),sQuery(id+"F0.wireOp",EDGE,"E115"),sQuery(id+"F0.wireOp",EDGE,"E116"),sQuery(id+"F0.wireOp",EDGE,"E118"),sQuery(id+"F0.wireOp",EDGE,"E119"),sQuery(id+"F0.wireOp",EDGE,"E120"),sQuery(id+"F0.wireOp",EDGE,"E121"),sQuery(id+"F0.wireOp",EDGE,"E122"),sQuery(id+"F0.wireOp",EDGE,"E123"),sQuery(id+"F0.wireOp",EDGE,"E124"),sQuery(id+"F0.wireOp",EDGE,"E125"),sQuery(id+"F0.wireOp",EDGE,"E126"),sQuery(id+"F0.wireOp",EDGE,"E127"),sQuery(id+"F0.wireOp",EDGE,"E128"),sQuery(id+"F0.wireOp",EDGE,"E129"),sQuery(id+"F0.wireOp",EDGE,"E130"),sQuery(id+"F0.wireOp",EDGE,"E131"),sQuery(id+"F0.wireOp",EDGE,"E132"),sQuery(id+"F0.wireOp",EDGE,"E133"),sQuery(id+"F0.wireOp",EDGE,"E134"),sQuery(id+"F0.wireOp",EDGE,"E135"),sQuery(id+"F0.wireOp",EDGE,"E136"),sQuery(id+"F0.wireOp",EDGE,"E137"),sQuery(id+"F0.wireOp",EDGE,"E138"),sQuery(id+"F0.wireOp",EDGE,"E139"),sQuery(id+"F0.wireOp",EDGE,"E140"),sQuery(id+"F0.wireOp",EDGE,"E141"),sQuery(id+"F0.wireOp",EDGE,"E142"),sQuery(id+"F0.wireOp",EDGE,"E143"),sQuery(id+"F0.wireOp",EDGE,"E144"),sQuery(id+"F0.wireOp",EDGE,"E145"),sQuery(id+"F0.wireOp",EDGE,"E146"),sQuery(id+"F0.wireOp",EDGE,"E147"),sQuery(id+"F0.wireOp",EDGE,"E148"),sQuery(id+"F0.wireOp",EDGE,"E150"),sQuery(id+"F0.wireOp",EDGE,"E151"),sQuery(id+"F0.wireOp",EDGE,"E152"),sQuery(id+"F0.wireOp",EDGE,"E153"),sQuery(id+"F0.wireOp",EDGE,"E154"),sQuery(id+"F0.wireOp",EDGE,"E155"),sQuery(id+"F0.wireOp",EDGE,"E156"),sQuery(id+"F0.wireOp",EDGE,"E157"),sQuery(id+"F0.wireOp",EDGE,"E158"),sQuery(id+"F0.wireOp",EDGE,"E159"),sQuery(id+"F0.wireOp",EDGE,"E160"),sQuery(id+"F0.wireOp",EDGE,"E161"),sQuery(id+"F0.wireOp",EDGE,"E162"),sQuery(id+"F0.wireOp",EDGE,"E163"),sQuery(id+"F0.wireOp",EDGE,"E164"),sQuery(id+"F0.wireOp",EDGE,"E165"),sQuery(id+"F0.wireOp",EDGE,"E166"),sQuery(id+"F0.wireOp",EDGE,"E167"),sQuery(id+"F0.wireOp",EDGE,"E168"),sQuery(id+"F0.wireOp",EDGE,"E169"),sQuery(id+"F0.wireOp",EDGE,"E170"),sQuery(id+"F0.wireOp",EDGE,"E171"),sQuery(id+"F0.wireOp",EDGE,"E172"),sQuery(id+"F0.wireOp",EDGE,"E173"),sQuery(id+"F0.wireOp",EDGE,"E174"),sQuery(id+"F0.wireOp",EDGE,"E175"),sQuery(id+"F0.wireOp",EDGE,"E176"),sQuery(id+"F0.wireOp",EDGE,"E177"),sQuery(id+"F0.wireOp",EDGE,"E178"),sQuery(id+"F0.wireOp",EDGE,"E179"),sQuery(id+"F0.wireOp",EDGE,"E180"),sQuery(id+"F0.wireOp",EDGE,"E181"),sQuery(id+"F0.wireOp",EDGE,"E182"),sQuery(id+"F0.wireOp",EDGE,"E183"),sQuery(id+"F0.wireOp",EDGE,"E184"),sQuery(id+"F0.wireOp",EDGE,"E185"),sQuery(id+"F0.wireOp",EDGE,"E186"),sQuery(id+"F0.wireOp",EDGE,"E187"),sQuery(id+"F0.wireOp",EDGE,"E188"),sQuery(id+"F0.wireOp",EDGE,"E189"),sQuery(id+"F0.wireOp",EDGE,"E190"),sQuery(id+"F0.wireOp",EDGE,"E191"),sQuery(id+"F0.wireOp",EDGE,"E192"),sQuery(id+"F0.wireOp",EDGE,"E193"),sQuery(id+"F0.wireOp",EDGE,"E194"),sQuery(id+"F0.wireOp",EDGE,"E195"),sQuery(id+"F0.wireOp",EDGE,"E196"),sQuery(id+"F0.wireOp",EDGE,"E197"),sQuery(id+"F0.wireOp",EDGE,"E198"),sQuery(id+"F0.wireOp",EDGE,"E199"),sQuery(id+"F0.wireOp",EDGE,"E200"),sQuery(id+"F0.wireOp",EDGE,"E201"),sQuery(id+"F0.wireOp",EDGE,"E202"),sQuery(id+"F0.wireOp",EDGE,"E203"),sQuery(id+"F0.wireOp",EDGE,"E204"),sQuery(id+"F0.wireOp",EDGE,"E205"),sQuery(id+"F0.wireOp",EDGE,"E206"),sQuery(id+"F0.wireOp",EDGE,"E207"),sQuery(id+"F0.wireOp",EDGE,"E208"),sQuery(id+"F0.wireOp",EDGE,"E209"),sQuery(id+"F0.wireOp",EDGE,"E210"),sQuery(id+"F0.wireOp",EDGE,"E211"),sQuery(id+"F0.wireOp",EDGE,"E212"),sQuery(id+"F0.wireOp",EDGE,"E213"),sQuery(id+"F0.wireOp",EDGE,"E214"),sQuery(id+"F0.wireOp",EDGE,"E215"),sQuery(id+"F0.wireOp",EDGE,"E216"),sQuery(id+"F0.wireOp",EDGE,"E217"),sQuery(id+"F0.wireOp",EDGE,"E218"),sQuery(id+"F0.wireOp",EDGE,"E219"),sQuery(id+"F0.wireOp",EDGE,"E220"),sQuery(id+"F0.wireOp",EDGE,"E221"),sQuery(id+"F0.wireOp",EDGE,"E222"),sQuery(id+"F0.wireOp",EDGE,"E223"),sQuery(id+"F0.wireOp",EDGE,"E224"),sQuery(id+"F0.wireOp",EDGE,"E225"),sQuery(id+"F0.wireOp",EDGE,"E226"),sQuery(id+"F0.wireOp",EDGE,"E227"),sQuery(id+"F0.wireOp",EDGE,"E228"),sQuery(id+"F0.wireOp",EDGE,"E229"),sQuery(id+"F0.wireOp",EDGE,"E230"),sQuery(id+"F0.wireOp",EDGE,"E231"),sQuery(id+"F0.wireOp",EDGE,"E232"),sQuery(id+"F0.wireOp",EDGE,"E233"),sQuery(id+"F0.wireOp",EDGE,"E234"),sQuery(id+"F0.wireOp",EDGE,"E235"),sQuery(id+"F0.wireOp",EDGE,"E236"),sQuery(id+"F0.wireOp",EDGE,"E237"),sQuery(id+"F0.wireOp",EDGE,"E238"),sQuery(id+"F0.wireOp",EDGE,"E239"),sQuery(id+"F0.wireOp",EDGE,"E240"),sQuery(id+"F0.wireOp",EDGE,"E241"),sQuery(id+"F0.wireOp",EDGE,"E242"),sQuery(id+"F0.wireOp",EDGE,"E243"),sQuery(id+"F0.wireOp",EDGE,"E244"),sQuery(id+"F0.wireOp",EDGE,"E245"),sQuery(id+"F0.wireOp",EDGE,"E246"),sQuery(id+"F0.wireOp",EDGE,"E247"),sQuery(id+"F0.wireOp",EDGE,"E248"),sQuery(id+"F0.wireOp",EDGE,"E249"),sQuery(id+"F0.wireOp",EDGE,"E250"),sQuery(id+"F0.wireOp",EDGE,"E251"),sQuery(id+"F0.wireOp",EDGE,"E252"),sQuery(id+"F0.wireOp",EDGE,"E253"),sQuery(id+"F0.wireOp",EDGE,"E254"),sQuery(id+"F0.wireOp",EDGE,"E255"),sQuery(id+"F0.wireOp",EDGE,"E256"),sQuery(id+"F0.wireOp",EDGE,"E257"),sQuery(id+"F0.wireOp",EDGE,"E258"),sQuery(id+"F0.wireOp",EDGE,"E259"),sQuery(id+"F0.wireOp",EDGE,"E260"),sQuery(id+"F0.wireOp",EDGE,"E262"),sQuery(id+"F0.wireOp",EDGE,"E263"),sQuery(id+"F0.wireOp",EDGE,"E264"),sQuery(id+"F0.wireOp",EDGE,"E265"),sQuery(id+"F0.wireOp",EDGE,"E266"),sQuery(id+"F0.wireOp",EDGE,"E267"),sQuery(id+"F0.wireOp",EDGE,"E268"),sQuery(id+"F0.wireOp",EDGE,"E269"),sQuery(id+"F0.wireOp",EDGE,"E270"),sQuery(id+"F0.wireOp",EDGE,"E271"),sQuery(id+"F0.wireOp",EDGE,"E272"),sQuery(id+"F0.wireOp",EDGE,"E273"),sQuery(id+"F0.wireOp",EDGE,"E274"),sQuery(id+"F0.wireOp",EDGE,"E275"),sQuery(id+"F0.wireOp",EDGE,"E276"),sQuery(id+"F0.wireOp",EDGE,"E277"),sQuery(id+"F0.wireOp",EDGE,"E278"),sQuery(id+"F0.wireOp",EDGE,"E279"),sQuery(id+"F0.wireOp",EDGE,"E280"),sQuery(id+"F0.wireOp",EDGE,"E281"),sQuery(id+"F0.wireOp",EDGE,"E282"),sQuery(id+"F0.wireOp",EDGE,"E283"),sQuery(id+"F0.wireOp",EDGE,"E284"),sQuery(id+"F0.wireOp",EDGE,"E285"),sQuery(id+"F0.wireOp",EDGE,"E286"),sQuery(id+"F0.wireOp",EDGE,"E287"),sQuery(id+"F0.wireOp",EDGE,"E288"),sQuery(id+"F0.wireOp",EDGE,"E289"),sQuery(id+"F0.wireOp",EDGE,"E290"),sQuery(id+"F0.wireOp",EDGE,"E291"),sQuery(id+"F0.wireOp",EDGE,"E292"),sQuery(id+"F0.wireOp",EDGE,"E293"),sQuery(id+"F0.wireOp",EDGE,"E294"),sQuery(id+"F0.wireOp",EDGE,"E295"),sQuery(id+"F0.wireOp",EDGE,"E296"),sQuery(id+"F0.wireOp",EDGE,"E297"),sQuery(id+"F0.wireOp",EDGE,"E298"),sQuery(id+"F0.wireOp",EDGE,"E299"),sQuery(id+"F0.wireOp",EDGE,"E300"),sQuery(id+"F0.wireOp",EDGE,"E301"),sQuery(id+"F0.wireOp",EDGE,"E302"),sQuery(id+"F0.wireOp",EDGE,"E303"),sQuery(id+"F0.wireOp",EDGE,"E304"),sQuery(id+"F0.wireOp",EDGE,"E305"),sQuery(id+"F0.wireOp",EDGE,"E306"),sQuery(id+"F0.wireOp",EDGE,"E307"),sQuery(id+"F0.wireOp",EDGE,"E308"),sQuery(id+"F0.wireOp",EDGE,"E309"),sQuery(id+"F0.wireOp",EDGE,"E310"),sQuery(id+"F0.wireOp",EDGE,"E311"),sQuery(id+"F0.wireOp",EDGE,"E312"),sQuery(id+"F0.wireOp",EDGE,"E313"),sQuery(id+"F0.wireOp",EDGE,"E314"),sQuery(id+"F0.wireOp",EDGE,"E315"),sQuery(id+"F0.wireOp",EDGE,"E316"),sQuery(id+"F0.wireOp",EDGE,"E317"),sQuery(id+"F0.wireOp",EDGE,"E318"),sQuery(id+"F0.wireOp",EDGE,"E319"),sQuery(id+"F0.wireOp",EDGE,"E320"),sQuery(id+"F0.wireOp",EDGE,"E321"),sQuery(id+"F0.wireOp",EDGE,"E322"),sQuery(id+"F0.wireOp",EDGE,"E323"),sQuery(id+"F0.wireOp",EDGE,"E324"),sQuery(id+"F0.wireOp",EDGE,"E325"),sQuery(id+"F0.wireOp",EDGE,"E326"),sQuery(id+"F0.wireOp",EDGE,"E327"),sQuery(id+"F0.wireOp",EDGE,"E328"),sQuery(id+"F0.wireOp",EDGE,"E329"),sQuery(id+"F0.wireOp",EDGE,"E330"),sQuery(id+"F0.wireOp",EDGE,"E331"),sQuery(id+"F0.wireOp",EDGE,"E332"),sQuery(id+"F0.wireOp",EDGE,"E333"),sQuery(id+"F0.wireOp",EDGE,"E334"),sQuery(id+"F0.wireOp",EDGE,"E335"),sQuery(id+"F0.wireOp",EDGE,"E336"),sQuery(id+"F0.wireOp",EDGE,"E337"),sQuery(id+"F0.wireOp",EDGE,"E338"),sQuery(id+"F0.wireOp",EDGE,"E339"),sQuery(id+"F0.wireOp",EDGE,"E340"),sQuery(id+"F0.wireOp",EDGE,"E341"),sQuery(id+"F0.wireOp",EDGE,"E342"),sQuery(id+"F0.wireOp",EDGE,"E343"),sQuery(id+"F0.wireOp",EDGE,"E344"),sQuery(id+"F0.wireOp",EDGE,"E345"),sQuery(id+"F0.wireOp",EDGE,"E346"),sQuery(id+"F0.wireOp",EDGE,"E347"),sQuery(id+"F0.wireOp",EDGE,"E348"),sQuery(id+"F0.wireOp",EDGE,"E349"),sQuery(id+"F0.wireOp",EDGE,"E350"),sQuery(id+"F0.wireOp",EDGE,"E351"),sQuery(id+"F0.wireOp",EDGE,"E352"),sQuery(id+"F0.wireOp",EDGE,"E353"),sQuery(id+"F0.wireOp",EDGE,"E354"),sQuery(id+"F0.wireOp",EDGE,"E355"),sQuery(id+"F0.wireOp",EDGE,"E356"),sQuery(id+"F0.wireOp",EDGE,"E357"),sQuery(id+"F0.wireOp",EDGE,"E358"),sQuery(id+"F0.wireOp",EDGE,"E359"),sQuery(id+"F0.wireOp",EDGE,"E360"),sQuery(id+"F0.wireOp",EDGE,"E361"),sQuery(id+"F0.wireOp",EDGE,"E362"),sQuery(id+"F0.wireOp",EDGE,"E363"),sQuery(id+"F0.wireOp",EDGE,"E364"),sQuery(id+"F0.wireOp",EDGE,"E365"),sQuery(id+"F0.wireOp",EDGE,"E366"),sQuery(id+"F0.wireOp",EDGE,"E367"),sQuery(id+"F0.wireOp",EDGE,"E368"),sQuery(id+"F0.wireOp",EDGE,"E369"),sQuery(id+"F0.wireOp",EDGE,"E370"),sQuery(id+"F0.wireOp",EDGE,"E371"),sQuery(id+"F0.wireOp",EDGE,"E372"),sQuery(id+"F0.wireOp",EDGE,"E373"),sQuery(id+"F0.wireOp",EDGE,"E374"),sQuery(id+"F0.wireOp",EDGE,"E375"),sQuery(id+"F0.wireOp",EDGE,"E376"),sQuery(id+"F0.wireOp",EDGE,"E377"),sQuery(id+"F0.wireOp",EDGE,"E378"),sQuery(id+"F0.wireOp",EDGE,"E379"),sQuery(id+"F0.wireOp",EDGE,"E380"),sQuery(id+"F0.wireOp",EDGE,"E381"),sQuery(id+"F0.wireOp",EDGE,"E382"),sQuery(id+"F0.wireOp",EDGE,"E383"),sQuery(id+"F0.wireOp",EDGE,"E384"),sQuery(id+"F0.wireOp",EDGE,"E385"),sQuery(id+"F0.wireOp",EDGE,"E386"),sQuery(id+"F0.wireOp",EDGE,"E387"),sQuery(id+"F0.wireOp",EDGE,"E388"),sQuery(id+"F0.wireOp",EDGE,"E389"),sQuery(id+"F0.wireOp",EDGE,"E390"),sQuery(id+"F0.wireOp",EDGE,"E391"),sQuery(id+"F0.wireOp",EDGE,"E392"),sQuery(id+"F0.wireOp",EDGE,"E393"),sQuery(id+"F0.wireOp",EDGE,"E394"),sQuery(id+"F0.wireOp",EDGE,"E395"),sQuery(id+"F0.wireOp",EDGE,"E396"),sQuery(id+"F0.wireOp",EDGE,"E397"),sQuery(id+"F0.wireOp",EDGE,"E398"),sQuery(id+"F0.wireOp",EDGE,"E399"),sQuery(id+"F0.wireOp",EDGE,"E400"),sQuery(id+"F0.wireOp",EDGE,"E401"),sQuery(id+"F0.wireOp",EDGE,"E402"),sQuery(id+"F0.wireOp",EDGE,"E403"),sQuery(id+"F0.wireOp",EDGE,"E404"),sQuery(id+"F0.wireOp",EDGE,"E405"),sQuery(id+"F0.wireOp",EDGE,"E407"),sQuery(id+"F0.wireOp",EDGE,"E408"),sQuery(id+"F0.wireOp",EDGE,"E409"),sQuery(id+"F0.wireOp",EDGE,"E410"),sQuery(id+"F0.wireOp",EDGE,"E411"),sQuery(id+"F0.wireOp",EDGE,"E412"),sQuery(id+"F0.wireOp",EDGE,"E413"),sQuery(id+"F0.wireOp",EDGE,"E414"),sQuery(id+"F0.wireOp",EDGE,"E415"),sQuery(id+"F0.wireOp",EDGE,"E416"),sQuery(id+"F0.wireOp",EDGE,"E417"),sQuery(id+"F0.wireOp",EDGE,"E418"),sQuery(id+"F0.wireOp",EDGE,"E419"),sQuery(id+"F0.wireOp",EDGE,"E420"),sQuery(id+"F0.wireOp",EDGE,"E421"),sQuery(id+"F0.wireOp",EDGE,"E422"),sQuery(id+"F0.wireOp",EDGE,"E423"),sQuery(id+"F0.wireOp",EDGE,"E424"),sQuery(id+"F0.wireOp",EDGE,"E425"),sQuery(id+"F0.wireOp",EDGE,"E426"),sQuery(id+"F0.wireOp",EDGE,"E427"),sQuery(id+"F0.wireOp",EDGE,"E428"),sQuery(id+"F0.wireOp",EDGE,"E429"),sQuery(id+"F0.wireOp",EDGE,"E430"),sQuery(id+"F0.wireOp",EDGE,"E431"),sQuery(id+"F0.wireOp",EDGE,"E432"),sQuery(id+"F0.wireOp",EDGE,"E433"),sQuery(id+"F0.wireOp",EDGE,"E434"),sQuery(id+"F0.wireOp",EDGE,"E435"),sQuery(id+"F0.wireOp",EDGE,"E436"),sQuery(id+"F0.wireOp",EDGE,"E437"),sQuery(id+"F0.wireOp",EDGE,"E438"),sQuery(id+"F0.wireOp",EDGE,"E439"),sQuery(id+"F0.wireOp",EDGE,"E440"),sQuery(id+"F0.wireOp",EDGE,"E441"),sQuery(id+"F0.wireOp",EDGE,"E442"),sQuery(id+"F0.wireOp",EDGE,"E443"),sQuery(id+"F0.wireOp",EDGE,"E444"),sQuery(id+"F0.wireOp",EDGE,"E445"),sQuery(id+"F0.wireOp",EDGE,"E446"),sQuery(id+"F0.wireOp",EDGE,"E447"),sQuery(id+"F0.wireOp",EDGE,"E448"),sQuery(id+"F0.wireOp",EDGE,"E449"),sQuery(id+"F0.wireOp",EDGE,"E450"),sQuery(id+"F0.wireOp",EDGE,"E451"),sQuery(id+"F0.wireOp",EDGE,"E452"),sQuery(id+"F0.wireOp",EDGE,"E453"),sQuery(id+"F0.wireOp",EDGE,"E454"),sQuery(id+"F0.wireOp",EDGE,"E455"),sQuery(id+"F0.wireOp",EDGE,"E456"),sQuery(id+"F0.wireOp",EDGE,"E457"),sQuery(id+"F0.wireOp",EDGE,"E458"),sQuery(id+"F0.wireOp",EDGE,"E459"),sQuery(id+"F0.wireOp",EDGE,"E460"),sQuery(id+"F0.wireOp",EDGE,"E461"),sQuery(id+"F0.wireOp",EDGE,"E462"),sQuery(id+"F0.wireOp",EDGE,"E463"),sQuery(id+"F0.wireOp",EDGE,"E464"),sQuery(id+"F0.wireOp",EDGE,"E466"),sQuery(id+"F0.wireOp",EDGE,"E467"),sQuery(id+"F0.wireOp",EDGE,"E468"),sQuery(id+"F0.wireOp",EDGE,"E469"),sQuery(id+"F0.wireOp",EDGE,"E470"),sQuery(id+"F0.wireOp",EDGE,"E471"),sQuery(id+"F0.wireOp",EDGE,"E472"),sQuery(id+"F0.wireOp",EDGE,"E473"),sQuery(id+"F0.wireOp",EDGE,"E474"),sQuery(id+"F0.wireOp",EDGE,"E475"),sQuery(id+"F0.wireOp",EDGE,"E476"),sQuery(id+"F0.wireOp",EDGE,"E477"),sQuery(id+"F0.wireOp",EDGE,"E478"),sQuery(id+"F0.wireOp",EDGE,"E479"),sQuery(id+"F0.wireOp",EDGE,"E480"),sQuery(id+"F0.wireOp",EDGE,"E481"),sQuery(id+"F0.wireOp",EDGE,"E482"),sQuery(id+"F0.wireOp",EDGE,"E483"),sQuery(id+"F0.wireOp",EDGE,"E484"),sQuery(id+"F0.wireOp",EDGE,"E485"),sQuery(id+"F0.wireOp",EDGE,"E486"),sQuery(id+"F0.wireOp",EDGE,"E487"),sQuery(id+"F0.wireOp",EDGE,"E488"),sQuery(id+"F0.wireOp",EDGE,"E489"),sQuery(id+"F0.wireOp",EDGE,"E490"),sQuery(id+"F0.wireOp",EDGE,"E491"),sQuery(id+"F0.wireOp",EDGE,"E492"),sQuery(id+"F0.wireOp",EDGE,"E493"),sQuery(id+"F0.wireOp",EDGE,"E494"),sQuery(id+"F0.wireOp",EDGE,"E495"),sQuery(id+"F0.wireOp",EDGE,"E496"),sQuery(id+"F0.wireOp",EDGE,"E498"),sQuery(id+"F0.wireOp",EDGE,"E499"),sQuery(id+"F0.wireOp",EDGE,"E500"),sQuery(id+"F0.wireOp",EDGE,"E501"),sQuery(id+"F0.wireOp",EDGE,"E502"),sQuery(id+"F0.wireOp",EDGE,"E503"),sQuery(id+"F0.wireOp",EDGE,"E504"),sQuery(id+"F0.wireOp",EDGE,"E505"),sQuery(id+"F0.wireOp",EDGE,"E506"),sQuery(id+"F0.wireOp",EDGE,"E507"),sQuery(id+"F0.wireOp",EDGE,"E508"),sQuery(id+"F0.wireOp",EDGE,"E509"),sQuery(id+"F0.wireOp",EDGE,"E510"),sQuery(id+"F0.wireOp",EDGE,"E511"),sQuery(id+"F0.wireOp",EDGE,"E512"),sQuery(id+"F0.wireOp",EDGE,"E513"),sQuery(id+"F0.wireOp",EDGE,"E514"),sQuery(id+"F0.wireOp",EDGE,"E515"),sQuery(id+"F0.wireOp",EDGE,"E516"),sQuery(id+"F0.wireOp",EDGE,"E517"),sQuery(id+"F0.wireOp",EDGE,"E518"),sQuery(id+"F0.wireOp",EDGE,"E519"),sQuery(id+"F0.wireOp",EDGE,"E520"),sQuery(id+"F0.wireOp",EDGE,"E521"),sQuery(id+"F0.wireOp",EDGE,"E522"),sQuery(id+"F0.wireOp",EDGE,"E523"),sQuery(id+"F0.wireOp",EDGE,"E524"),sQuery(id+"F0.wireOp",EDGE,"E525"),sQuery(id+"F0.wireOp",EDGE,"E526"),sQuery(id+"F0.wireOp",EDGE,"E527"),sQuery(id+"F0.wireOp",EDGE,"E528"),sQuery(id+"F0.wireOp",EDGE,"E529"),sQuery(id+"F0.wireOp",EDGE,"E530"),sQuery(id+"F0.wireOp",EDGE,"E531"),sQuery(id+"F0.wireOp",EDGE,"E532"),sQuery(id+"F0.wireOp",EDGE,"E533"),sQuery(id+"F0.wireOp",EDGE,"E534"),sQuery(id+"F0.wireOp",EDGE,"E535"),sQuery(id+"F0.wireOp",EDGE,"E536"),sQuery(id+"F0.wireOp",EDGE,"E537"),sQuery(id+"F0.wireOp",EDGE,"E538"),sQuery(id+"F0.wireOp",EDGE,"E539"),sQuery(id+"F0.wireOp",EDGE,"E540"),sQuery(id+"F0.wireOp",EDGE,"E541"),sQuery(id+"F0.wireOp",EDGE,"E542"),sQuery(id+"F0.wireOp",EDGE,"E543"),sQuery(id+"F0.wireOp",EDGE,"E544"),sQuery(id+"F0.wireOp",EDGE,"E545"),sQuery(id+"F0.wireOp",EDGE,"E546"),sQuery(id+"F0.wireOp",EDGE,"E547"),sQuery(id+"F0.wireOp",EDGE,"E548"),sQuery(id+"F0.wireOp",EDGE,"E549"),sQuery(id+"F0.wireOp",EDGE,"E550"),sQuery(id+"F0.wireOp",EDGE,"E551"),sQuery(id+"F0.wireOp",EDGE,"E552"),sQuery(id+"F0.wireOp",EDGE,"E553"),sQuery(id+"F0.wireOp",EDGE,"E554"),sQuery(id+"F0.wireOp",EDGE,"E555"),sQuery(id+"F0.wireOp",EDGE,"E556"),sQuery(id+"F0.wireOp",EDGE,"E557"),sQuery(id+"F0.wireOp",EDGE,"E558"),sQuery(id+"F0.wireOp",EDGE,"E559"),sQuery(id+"F0.wireOp",EDGE,"E560"),sQuery(id+"F0.wireOp",EDGE,"E561"),sQuery(id+"F0.wireOp",EDGE,"E562"),sQuery(id+"F0.wireOp",EDGE,"E563"),sQuery(id+"F0.wireOp",EDGE,"E564"),sQuery(id+"F0.wireOp",EDGE,"E565"),sQuery(id+"F0.wireOp",EDGE,"E566"),sQuery(id+"F0.wireOp",EDGE,"E567"),sQuery(id+"F0.wireOp",EDGE,"E568"),sQuery(id+"F0.wireOp",EDGE,"E569"),sQuery(id+"F0.wireOp",EDGE,"E570"),sQuery(id+"F0.wireOp",EDGE,"E571"),sQuery(id+"F0.wireOp",EDGE,"E572"),sQuery(id+"F0.wireOp",EDGE,"E573"),sQuery(id+"F0.wireOp",EDGE,"E597"),sQuery(id+"F0.wireOp",EDGE,"E598"),sQuery(id+"F0.wireOp",EDGE,"E599"),sQuery(id+"F0.wireOp",EDGE,"E600"),sQuery(id+"F0.wireOp",EDGE,"E601"),sQuery(id+"F0.wireOp",EDGE,"E602"),sQuery(id+"F0.wireOp",EDGE,"E603"),sQuery(id+"F0.wireOp",EDGE,"E604"),sQuery(id+"F0.wireOp",EDGE,"E605"),sQuery(id+"F0.wireOp",EDGE,"E606"),sQuery(id+"F0.wireOp",EDGE,"E607"),sQuery(id+"F0.wireOp",EDGE,"E608"),sQuery(id+"F0.wireOp",EDGE,"E609"),sQuery(id+"F0.wireOp",EDGE,"E610"),sQuery(id+"F0.wireOp",EDGE,"E611"),sQuery(id+"F0.wireOp",EDGE,"E612"),sQuery(id+"F0.wireOp",EDGE,"E613"),sQuery(id+"F0.wireOp",EDGE,"E614"),sQuery(id+"F0.wireOp",EDGE,"E615"),sQuery(id+"F0.wireOp",EDGE,"E616"),sQuery(id+"F0.wireOp",EDGE,"E617"),sQuery(id+"F0.wireOp",EDGE,"E618"),sQuery(id+"F0.wireOp",EDGE,"E619"),sQuery(id+"F0.wireOp",EDGE,"E620"),sQuery(id+"F0.wireOp",EDGE,"E621"),sQuery(id+"F0.wireOp",EDGE,"E622"),sQuery(id+"F0.wireOp",EDGE,"E623"),sQuery(id+"F0.wireOp",EDGE,"E624"),sQuery(id+"F0.wireOp",EDGE,"E625"),sQuery(id+"F0.wireOp",EDGE,"E626"),sQuery(id+"F0.wireOp",EDGE,"E627"),sQuery(id+"F0.wireOp",EDGE,"E628"),sQuery(id+"F0.wireOp",EDGE,"E629"),sQuery(id+"F0.wireOp",EDGE,"E630"),sQuery(id+"F0.wireOp",EDGE,"E631"),sQuery(id+"F0.wireOp",EDGE,"E632"),sQuery(id+"F0.wireOp",EDGE,"E633"),sQuery(id+"F0.wireOp",EDGE,"E634"),sQuery(id+"F0.wireOp",EDGE,"E635"),sQuery(id+"F0.wireOp",EDGE,"E636"),sQuery(id+"F0.wireOp",EDGE,"E637"),sQuery(id+"F0.wireOp",EDGE,"E638"),sQuery(id+"F0.wireOp",EDGE,"E639"),sQuery(id+"F0.wireOp",EDGE,"E640"),sQuery(id+"F0.wireOp",EDGE,"E641"),sQuery(id+"F0.wireOp",EDGE,"E642"),sQuery(id+"F0.wireOp",EDGE,"E643"),sQuery(id+"F0.wireOp",EDGE,"E644"),sQuery(id+"F0.wireOp",EDGE,"E645"),sQuery(id+"F0.wireOp",EDGE,"E646"),sQuery(id+"F0.wireOp",EDGE,"E647"),sQuery(id+"F0.wireOp",EDGE,"E648"),sQuery(id+"F0.wireOp",EDGE,"E649"),sQuery(id+"F0.wireOp",EDGE,"E650"),sQuery(id+"F0.wireOp",EDGE,"E651"),sQuery(id+"F0.wireOp",EDGE,"E652"),sQuery(id+"F0.wireOp",EDGE,"E653"),sQuery(id+"F0.wireOp",EDGE,"E654"),sQuery(id+"F0.wireOp",EDGE,"E655"),sQuery(id+"F0.wireOp",EDGE,"E656"),sQuery(id+"F0.wireOp",EDGE,"E657"),sQuery(id+"F0.wireOp",EDGE,"E658"),sQuery(id+"F0.wireOp",EDGE,"E659"),sQuery(id+"F0.wireOp",EDGE,"E660"),sQuery(id+"F0.wireOp",EDGE,"E661"),sQuery(id+"F0.wireOp",EDGE,"E662"),sQuery(id+"F0.wireOp",EDGE,"E663"),sQuery(id+"F0.wireOp",EDGE,"E664"),sQuery(id+"F0.wireOp",EDGE,"E665"),sQuery(id+"F0.wireOp",EDGE,"E666"),sQuery(id+"F0.wireOp",EDGE,"E667"),sQuery(id+"F0.wireOp",EDGE,"E668"),sQuery(id+"F0.wireOp",EDGE,"E669"),sQuery(id+"F0.wireOp",EDGE,"E670"),sQuery(id+"F0.wireOp",EDGE,"E672"),sQuery(id+"F0.wireOp",EDGE,"E673"),sQuery(id+"F0.wireOp",EDGE,"E675"),sQuery(id+"F0.wireOp",EDGE,"E676"),sQuery(id+"F0.wireOp",EDGE,"E677"),sQuery(id+"F0.wireOp",EDGE,"E678"),sQuery(id+"F0.wireOp",EDGE,"E679"),sQuery(id+"F0.wireOp",EDGE,"E680"),sQuery(id+"F0.wireOp",EDGE,"E681"),sQuery(id+"F0.wireOp",EDGE,"E682"),sQuery(id+"F0.wireOp",EDGE,"E683"),sQuery(id+"F0.wireOp",EDGE,"E684"),sQuery(id+"F0.wireOp",EDGE,"E685"),sQuery(id+"F0.wireOp",EDGE,"E686"),sQuery(id+"F0.wireOp",EDGE,"E687"),sQuery(id+"F0.wireOp",EDGE,"E688"),sQuery(id+"F0.wireOp",EDGE,"E689"),sQuery(id+"F0.wireOp",EDGE,"E690"),sQuery(id+"F0.wireOp",EDGE,"E691"),sQuery(id+"F0.wireOp",EDGE,"E692"),sQuery(id+"F0.wireOp",EDGE,"E693"),sQuery(id+"F0.wireOp",EDGE,"E694"),sQuery(id+"F0.wireOp",EDGE,"E574"),sQuery(id+"F0.wireOp",EDGE,"E575"),sQuery(id+"F0.wireOp",EDGE,"E576"),sQuery(id+"F0.wireOp",EDGE,"E577"),sQuery(id+"F0.wireOp",EDGE,"E578"),sQuery(id+"F0.wireOp",EDGE,"E579"),sQuery(id+"F0.wireOp",EDGE,"E580"),sQuery(id+"F0.wireOp",EDGE,"E581"),sQuery(id+"F0.wireOp",EDGE,"E582"),sQuery(id+"F0.wireOp",EDGE,"E583"),sQuery(id+"F0.wireOp",EDGE,"E584"),sQuery(id+"F0.wireOp",EDGE,"E585"),sQuery(id+"F0.wireOp",EDGE,"E708"),sQuery(id+"F0.wireOp",EDGE,"E736"),sQuery(id+"F0.wireOp",EDGE,"E586"),sQuery(id+"F0.wireOp",EDGE,"E587"),sQuery(id+"F0.wireOp",EDGE,"E739"),sQuery(id+"F0.wireOp",EDGE,"E741"),sQuery(id+"F0.wireOp",EDGE,"E589"),sQuery(id+"F0.wireOp",EDGE,"E742"),sQuery(id+"F0.wireOp",EDGE,"E590"),sQuery(id+"F0.wireOp",EDGE,"E743"),sQuery(id+"F0.wireOp",EDGE,"E745"),sQuery(id+"F0.wireOp",EDGE,"E746"),sQuery(id+"F0.wireOp",EDGE,"E592"),sQuery(id+"F0.wireOp",EDGE,"E593"),sQuery(id+"F0.wireOp",EDGE,"E748"),sQuery(id+"F0.wireOp",EDGE,"E594"),sQuery(id+"F0.wireOp",EDGE,"E595"),sQuery(id+"F0.wireOp",EDGE,"E749"),sQuery(id+"F0.wireOp",EDGE,"E751"),sQuery(id+"F0.wireOp",EDGE,"E752"),sQuery(id+"F0.wireOp",EDGE,"E596"),sQuery(id+"F0.wireOp",EDGE,"E737"),sQuery(id+"F0.wireOp",EDGE,"E753.trimOffspring"),sQuery(id+"F0.wireOp",EDGE,"E754.trimOffspring"),sQuery(id+"F0.wireOp",EDGE,"E703"),sQuery(id+"F0.wireOp",EDGE,"E702"),sQuery(id+"F0.wireOp",EDGE,"E704"),sQuery(id+"F0.wireOp",EDGE,"E705"),sQuery(id+"F0.wireOp",EDGE,"E706"),sQuery(id+"F0.wireOp",EDGE,"E707"),sQuery(id+"F0.wireOp",EDGE,"E709"),sQuery(id+"F0.wireOp",EDGE,"E710"),sQuery(id+"F0.wireOp",EDGE,"E711"),sQuery(id+"F0.wireOp",EDGE,"E712"),sQuery(id+"F0.wireOp",EDGE,"E713"),sQuery(id+"F0.wireOp",EDGE,"E714"),sQuery(id+"F0.wireOp",EDGE,"E750"),sQuery(id+"F0.wireOp",EDGE,"E715"),sQuery(id+"F0.wireOp",EDGE,"E716"),sQuery(id+"F0.wireOp",EDGE,"E717"),sQuery(id+"F0.wireOp",EDGE,"E718"),sQuery(id+"F0.wireOp",EDGE,"E719"),sQuery(id+"F0.wireOp",EDGE,"E720"),sQuery(id+"F0.wireOp",EDGE,"E721"),sQuery(id+"F0.wireOp",EDGE,"E755.trimOffspring"),sQuery(id+"F0.wireOp",EDGE,"E744"),sQuery(id+"F0.wireOp",EDGE,"E756.trimOffspring"),sQuery(id+"F0.wireOp",EDGE,"E757.trimOffspring"),sQuery(id+"F0.wireOp",EDGE,"E758.trimOffspring"),sQuery(id+"F0.wireOp",EDGE,"E759.trimOffspring"),sQuery(id+"F0.wireOp",EDGE,"E760.trimOffspring"),sQuery(id+"F0.wireOp",EDGE,"E761.trimOffspring"),sQuery(id+"F0.wireOp",EDGE,"E762.trimOffspring"),sQuery(id+"F0.wireOp",EDGE,"E763.trimOffspring"),sQuery(id+"F0.wireOp",EDGE,"E764.trimOffspring"),sQuery(id+"F0.wireOp",EDGE,"E765.trimOffspring"),sQuery(id+"F0.wireOp",EDGE,"E766.trimOffspring"),sQuery(id+"F0.wireOp",EDGE,"E767.trimOffspring"),sQuery(id+"F0.wireOp",EDGE,"E768.trimOffspring"),sQuery(id+"F0.wireOp",EDGE,"E769.trimOffspring"),sQuery(id+"F0.wireOp",EDGE,"E740"),sQuery(id+"F0.wireOp",EDGE,"E770.trimOffspring"),sQuery(id+"F0.wireOp",EDGE,"E771.trimOffspring"),sQuery(id+"F0.wireOp",EDGE,"E772.trimOffspring"),sQuery(id+"F0.wireOp",EDGE,"E773.trimOffspring"),sQuery(id+"F0.wireOp",EDGE,"E774.trimOffspring"),sQuery(id+"F0.wireOp",EDGE,"E775.trimOffspring"),sQuery(id+"F0.wireOp",EDGE,"E776.trimOffspring")])],"isStart":false});
            var sketch = newSketch(context, id + "F2", { "sketchPlane" : qUnion([Q0])});
            skLineSegment(sketch, "E777.bottom", {"start": v(-35.86, 40) * mm, "end": v(35.86, 40) * mm});
            skLineSegment(sketch, "E777.top", {"start": v(-35.86, -40) * mm, "end": v(35.86, -40) * mm});
            skLineSegment(sketch, "E777.left", {"start": v(-40, 35.86) * mm, "end": v(-40, -35.86) * mm});
            skLineSegment(sketch, "E777.right", {"start": v(40, 35.86) * mm, "end": v(40, -35.86) * mm});
            skPoint(sketch, "E777.middle", {"position": v(0, 0) * mm});
            skPoint(sketch, "E778.visualSharp", {"position": v(-40, 40) * mm});
            skArc(sketch, "E778.filletArc", {"start": v(-35.86, 40) * mm, "mid": v(-38.8, 38.8) * mm, "end": v(-40, 35.86) * mm});
            skPoint(sketch, "E779.visualSharp", {"position": v(40, 40) * mm});
            skArc(sketch, "E779.filletArc", {"start": v(40, 35.86) * mm, "mid": v(38.8, 38.8) * mm, "end": v(35.86, 40) * mm});
            skPoint(sketch, "E780.visualSharp", {"position": v(40, -40) * mm});
            skArc(sketch, "E780.filletArc", {"start": v(35.86, -40) * mm, "mid": v(38.8, -38.8) * mm, "end": v(40, -35.86) * mm});
            skPoint(sketch, "E781.visualSharp", {"position": v(-40, -40) * mm});
            skArc(sketch, "E781.filletArc", {"start": v(-40, -35.86) * mm, "mid": v(-38.8, -38.8) * mm, "end": v(-35.86, -40) * mm});
            skLineSegment(sketch, "E782.0", {"start": v(-35.86, 42.01) * mm, "end": v(35.86, 42.01) * mm});
            skLineSegment(sketch, "E782.1", {"start": v(-42.01, 35.86) * mm, "end": v(-42.01, -35.86) * mm});
            skLineSegment(sketch, "E782.2", {"start": v(-35.86, -42.01) * mm, "end": v(35.86, -42.01) * mm});
            skLineSegment(sketch, "E782.3", {"start": v(42.01, 35.86) * mm, "end": v(42.01, -35.86) * mm});
            skPoint(sketch, "E783.visualSharp", {"position": v(-42.01, 42.01) * mm});
            skArc(sketch, "E783.filletArc", {"start": v(-35.86, 42.01) * mm, "mid": v(-40.21, 40.21) * mm, "end": v(-42.01, 35.86) * mm});
            skPoint(sketch, "E784.visualSharp", {"position": v(42.01, 42.01) * mm});
            skArc(sketch, "E784.filletArc", {"start": v(42.01, 35.86) * mm, "mid": v(40.21, 40.21) * mm, "end": v(35.86, 42.01) * mm});
            skPoint(sketch, "E785.visualSharp", {"position": v(42.01, -42.01) * mm});
            skArc(sketch, "E785.filletArc", {"start": v(35.86, -42.01) * mm, "mid": v(40.21, -40.21) * mm, "end": v(42.01, -35.86) * mm});
            skPoint(sketch, "E786.visualSharp", {"position": v(-42.01, -42.01) * mm});
            skArc(sketch, "E786.filletArc", {"start": v(-42.01, -35.86) * mm, "mid": v(-40.21, -40.21) * mm, "end": v(-35.86, -42.01) * mm});
            skSolve(sketch);
        }
        {
            var Q0;
            Q0 = qSketchRegion(id + "F2", true);
            extrude(context, id + "F3", {"entities" : qUnion([Q0]), "operationType" : NewBodyOperationType.ADD, "oppositeDirection" : true, "depth" : 27.94 * mm, "offsetDistance" : 25.4 * mm});
        }
    });
